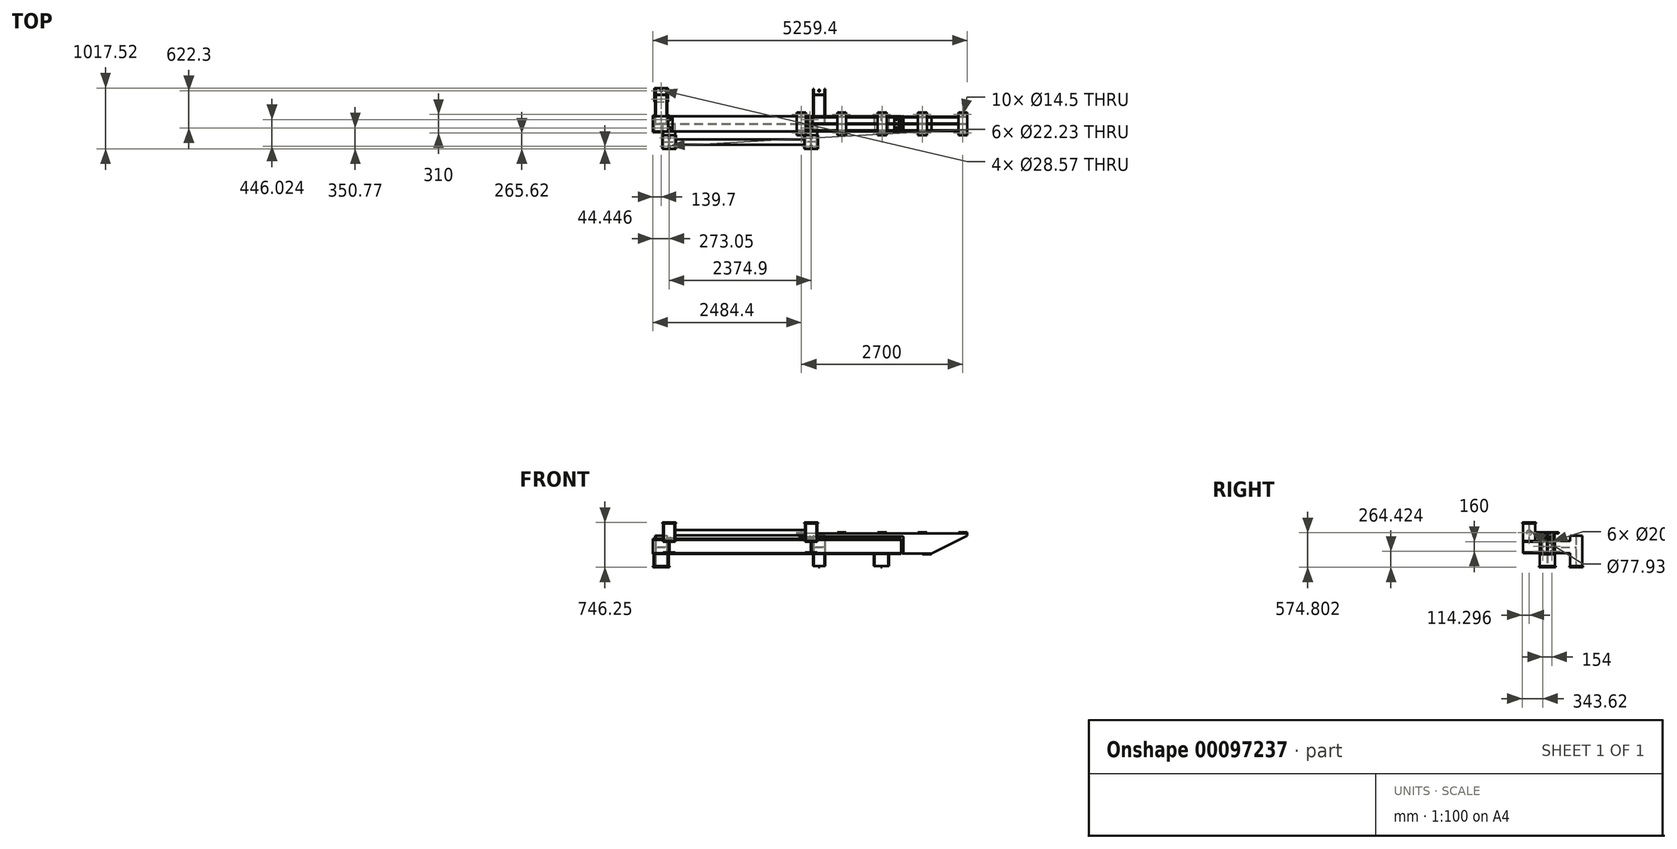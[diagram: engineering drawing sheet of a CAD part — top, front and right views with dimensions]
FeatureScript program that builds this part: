
annotation { "Feature Type Name" : "Feature", "Feature Type Description" : "" }
export const myFeature = defineFeature(function(context is Context, id is Id, definition is map)
    precondition{}
    {
        {
            var Q0;
            Q0=qCreatedBy(makeId("Top.planeOp"),FACE);
            var sketch = newSketch(context, id + "F0", { "sketchPlane" : qUnion([Q0])});
            skLineSegment(sketch, "E0.bottom", {"start": v(-1320.8, 241.3) * mm, "end": v(1320.8, 241.3) * mm, "construction": true});
            skLineSegment(sketch, "E0.top", {"start": v(-1320.8, -241.3) * mm, "end": v(1320.8, -241.3) * mm, "construction": true});
            skLineSegment(sketch, "E0.left", {"start": v(-1320.8, 241.3) * mm, "end": v(-1320.8, -241.3) * mm, "construction": true});
            skLineSegment(sketch, "E0.right", {"start": v(1320.8, 241.3) * mm, "end": v(1320.8, -241.3) * mm, "construction": true});
            skPoint(sketch, "E0.middle", {"position": v(0, 0) * mm});
            skLineSegment(sketch, "E1.bottom", {"start": v(-1435.1, 355.6) * mm, "end": v(-1206.5, 355.6) * mm});
            skLineSegment(sketch, "E1.top", {"start": v(-1435.1, 127) * mm, "end": v(-1206.5, 127) * mm});
            skLineSegment(sketch, "E1.left", {"start": v(-1435.1, 355.6) * mm, "end": v(-1435.1, 127) * mm});
            skLineSegment(sketch, "E1.right", {"start": v(-1206.5, 355.6) * mm, "end": v(-1206.5, 127) * mm});
            skPoint(sketch, "E1.middle", {"position": v(-1320.8, 241.3) * mm});
            skLineSegment(sketch, "E2", {"start": v(0, -413.23) * mm, "end": v(0, 639.03) * mm, "construction": true});
            skLineSegment(sketch, "E3", {"start": v(-1320.8, 355.6) * mm, "end": v(-1320.8, 127) * mm, "construction": true});
            skLineSegment(sketch, "E4", {"start": v(-1435.1, 241.3) * mm, "end": v(-1206.5, 241.3) * mm, "construction": true});
            skLineSegment(sketch, "E5.0", {"start": v(-1435.1, 311.15) * mm, "end": v(-1206.5, 311.15) * mm, "construction": true});
            skCircle(sketch, "E6", {"center": v(-1320.8, 311.15) * mm, "radius": 14.29 * mm});
            skCircle(sketch, "E7.MirrorC", {"center": v(-1320.8, 171.45) * mm, "radius": 14.29 * mm});
            skCircle(sketch, "E8.MirrorC", {"center": v(1320.8, 311.15) * mm, "radius": 14.29 * mm});
            skCircle(sketch, "E9.MirrorC", {"center": v(1320.8, 171.45) * mm, "radius": 14.29 * mm});
            skLineSegment(sketch, "E10.MirrorCS", {"start": v(1435.1, 311.15) * mm, "end": v(1206.5, 311.15) * mm, "construction": true});
            skLineSegment(sketch, "E11.MirrorCS", {"start": v(1435.1, 241.3) * mm, "end": v(1206.5, 241.3) * mm, "construction": true});
            skLineSegment(sketch, "E12.MirrorCS", {"start": v(1320.8, 355.6) * mm, "end": v(1320.8, 127) * mm, "construction": true});
            skLineSegment(sketch, "E13.MirrorCS", {"start": v(1435.1, 355.6) * mm, "end": v(1206.5, 355.6) * mm});
            skPoint(sketch, "E14.MirrorP", {"position": v(1320.8, 241.3) * mm});
            skLineSegment(sketch, "E15.MirrorCS", {"start": v(1206.5, 355.6) * mm, "end": v(1206.5, 127) * mm});
            skLineSegment(sketch, "E16.MirrorCS", {"start": v(1435.1, 127) * mm, "end": v(1206.5, 127) * mm});
            skLineSegment(sketch, "E17.MirrorCS", {"start": v(1435.1, 355.6) * mm, "end": v(1435.1, 127) * mm});
            skLineSegment(sketch, "E18.bottom", {"start": v(-1460.5, -381) * mm, "end": v(-1181.1, -381) * mm});
            skLineSegment(sketch, "E18.top", {"start": v(-1460.5, -101.6) * mm, "end": v(-1181.1, -101.6) * mm});
            skLineSegment(sketch, "E18.left", {"start": v(-1460.5, -381) * mm, "end": v(-1460.5, -101.6) * mm});
            skLineSegment(sketch, "E18.right", {"start": v(-1181.1, -381) * mm, "end": v(-1181.1, -101.6) * mm});
            skPoint(sketch, "E18.middle", {"position": v(-1320.8, -241.3) * mm});
            skLineSegment(sketch, "E19", {"start": v(-1320.8, -241.3) * mm, "end": v(-1460.5, -241.3) * mm, "construction": true});
            skLineSegment(sketch, "E20.0", {"start": v(-1320.8, -171.45) * mm, "end": v(-1460.5, -171.45) * mm, "construction": true});
            skCircle(sketch, "E21", {"center": v(-1320.8, -171.45) * mm, "radius": 14.29 * mm});
            skCircle(sketch, "E22.MirrorC", {"center": v(-1320.8, -311.15) * mm, "radius": 14.29 * mm});
            skLineSegment(sketch, "E23", {"start": v(-1320.8, -638.8) * mm, "end": v(-1320.8, -1011) * mm, "construction": true});
            skPoint(sketch, "E24.orphan", {"position": v(-1320.8, -381) * mm});
            skLineSegment(sketch, "E25.0", {"start": v(0, -638.8) * mm, "end": v(0, -1011) * mm, "construction": true});
            skLineSegment(sketch, "E26.0", {"start": v(1320.8, -638.8) * mm, "end": v(1320.8, -1011) * mm, "construction": true});
            skLineSegment(sketch, "E27.0", {"start": v(2362.2, -638.8) * mm, "end": v(2362.2, -1011) * mm, "construction": true});
            skLineSegment(sketch, "E28", {"start": v(-1320.8, -1011) * mm, "end": v(2362.2, -1011) * mm, "construction": true});
            skLineSegment(sketch, "E29", {"start": v(520.7, -1011) * mm, "end": v(520.7, -1354.57) * mm, "construction": true});
            skCircle(sketch, "E30.MirrorC", {"center": v(2362.2, -171.45) * mm, "radius": 14.29 * mm});
            skCircle(sketch, "E31.MirrorC", {"center": v(2362.2, -311.15) * mm, "radius": 14.29 * mm});
            skLineSegment(sketch, "E32.MirrorCS", {"start": v(2362.2, -171.45) * mm, "end": v(2501.9, -171.45) * mm, "construction": true});
            skLineSegment(sketch, "E33.MirrorCS", {"start": v(2501.9, -101.6) * mm, "end": v(2222.5, -101.6) * mm});
            skLineSegment(sketch, "E34.MirrorCS", {"start": v(2501.9, -381) * mm, "end": v(2222.5, -381) * mm});
            skLineSegment(sketch, "E35.MirrorCS", {"start": v(2362.2, -241.3) * mm, "end": v(2501.9, -241.3) * mm, "construction": true});
            skPoint(sketch, "E36.MirrorP", {"position": v(2362.2, -241.3) * mm});
            skLineSegment(sketch, "E37.MirrorCS", {"start": v(2222.5, -381) * mm, "end": v(2222.5, -101.6) * mm});
            skPoint(sketch, "E38.MirrorP", {"position": v(2362.2, -381) * mm});
            skLineSegment(sketch, "E39.MirrorCS", {"start": v(2501.9, -381) * mm, "end": v(2501.9, -101.6) * mm});
            skSolve(sketch);
        }
        {
            var Q0;
            Q0=makeQuery(id+"F0.imprint","IMPRINT",FACE,{"disambiguationData":[TD([[makeQuery(id+"F0.imprint","IMPRINT",EDGE,{"derivedFrom":sQuery(id+"F0.wireOp",EDGE,"E1.bottom")}),-1.0]])]});
            var Q1;
            Q1=makeQuery(id+"F0.imprint","IMPRINT",FACE,{"disambiguationData":[TD([[makeQuery(id+"F0.imprint","IMPRINT",EDGE,{"derivedFrom":sQuery(id+"F0.wireOp",EDGE,"E8.MirrorC")}),1.0]])]});
            var Q2;
            Q2=makeQuery(id+"F0.imprint","IMPRINT",FACE,{"disambiguationData":[TD([[makeQuery(id+"F0.imprint","IMPRINT",EDGE,{"derivedFrom":sQuery(id+"F0.wireOp",EDGE,"E30.MirrorC")}),1.0]])]});
            var Q3;
            Q3=makeQuery(id+"F0.imprint","IMPRINT",FACE,{"disambiguationData":[TD([[makeQuery(id+"F0.imprint","IMPRINT",EDGE,{"derivedFrom":sQuery(id+"F0.wireOp",EDGE,"E18.bottom")}),1.0]])]});
            extrude(context, id + "F1", {"entities" : qUnion([Q0, Q1, Q2, Q3]), "depth" : 19.05 * mm});
        }
        {
            var Q0;
            Q0=makeQuery(id+"F1.opExtrude","CAP_FACE",FACE,{"disambiguationData":[OSD([sQuery(id+"F0.wireOp",EDGE,"E1.bottom"),sQuery(id+"F0.wireOp",EDGE,"E1.top"),sQuery(id+"F0.wireOp",EDGE,"E1.left"),sQuery(id+"F0.wireOp",EDGE,"E1.right"),sQuery(id+"F0.wireOp",EDGE,"E6"),sQuery(id+"F0.wireOp",EDGE,"E7.MirrorC")])],"isStart":false});
            var sketch = newSketch(context, id + "F2", { "sketchPlane" : qUnion([Q0])});
            skLineSegment(sketch, "E40.0", {"start": v(-1435.1, 241.3) * mm, "end": v(-1206.5, 241.3) * mm, "construction": true});
            skLineSegment(sketch, "E41.0", {"start": v(-1320.8, 355.6) * mm, "end": v(-1320.8, 127) * mm, "construction": true});
            skLineSegment(sketch, "E42.bottom", {"start": v(-1422.4, 342.9) * mm, "end": v(-1411.35, 342.9) * mm});
            skLineSegment(sketch, "E42.top", {"start": v(-1422.4, 139.7) * mm, "end": v(-1411.35, 139.7) * mm});
            skLineSegment(sketch, "E42.left", {"start": v(-1422.4, 342.9) * mm, "end": v(-1422.4, 139.7) * mm});
            skLineSegment(sketch, "E42.right", {"start": v(-1219.2, 342.9) * mm, "end": v(-1219.2, 139.7) * mm, "construction": true});
            skPoint(sketch, "E42.middle", {"position": v(-1320.8, 241.3) * mm});
            skLineSegment(sketch, "E43.0", {"start": v(-1411.35, 342.9) * mm, "end": v(-1411.35, 251.27) * mm});
            skLineSegment(sketch, "E44.trimOffspring", {"start": v(-1405, 237.68) * mm, "end": v(-1320.8, 237.68) * mm});
            skLineSegment(sketch, "E45.MirrorCS", {"start": v(-1405, 244.92) * mm, "end": v(-1320.8, 244.92) * mm});
            skLineSegment(sketch, "E46.trimOffspring", {"start": v(-1411.35, 231.33) * mm, "end": v(-1411.35, 139.7) * mm});
            skPoint(sketch, "E47.visualSharp", {"position": v(-1411.35, 244.92) * mm});
            skArc(sketch, "E47.filletArc", {"start": v(-1411.35, 251.27) * mm, "mid": v(-1409.5, 246.78) * mm, "end": v(-1405, 244.92) * mm});
            skPoint(sketch, "E48.visualSharp", {"position": v(-1411.35, 237.68) * mm});
            skArc(sketch, "E48.filletArc", {"start": v(-1405, 237.68) * mm, "mid": v(-1409.5, 235.82) * mm, "end": v(-1411.35, 231.33) * mm});
            skArc(sketch, "E49.MirrorCS", {"start": v(-1236.6, 237.68) * mm, "mid": v(-1232.1, 235.82) * mm, "end": v(-1230.25, 231.33) * mm});
            skArc(sketch, "E50.MirrorCS", {"start": v(-1230.25, 251.27) * mm, "mid": v(-1232.1, 246.78) * mm, "end": v(-1236.6, 244.92) * mm});
            skPoint(sketch, "E51.MirrorP", {"position": v(-1230.25, 237.68) * mm});
            skPoint(sketch, "E52.MirrorP", {"position": v(-1230.25, 244.92) * mm});
            skLineSegment(sketch, "E53.MirrorCS", {"start": v(-1230.25, 342.9) * mm, "end": v(-1230.25, 251.27) * mm});
            skLineSegment(sketch, "E54.MirrorCS", {"start": v(-1236.6, 237.68) * mm, "end": v(-1320.8, 237.68) * mm});
            skLineSegment(sketch, "E55.MirrorCS", {"start": v(-1236.6, 244.92) * mm, "end": v(-1320.8, 244.92) * mm});
            skLineSegment(sketch, "E56.MirrorCS", {"start": v(-1219.2, 139.7) * mm, "end": v(-1230.25, 139.7) * mm});
            skLineSegment(sketch, "E57.MirrorCS", {"start": v(-1230.25, 231.33) * mm, "end": v(-1230.25, 139.7) * mm});
            skLineSegment(sketch, "E58.MirrorCS", {"start": v(-1219.2, 342.9) * mm, "end": v(-1230.25, 342.9) * mm});
            skLineSegment(sketch, "E59.MirrorCS", {"start": v(-1219.2, 342.9) * mm, "end": v(-1219.2, 139.7) * mm});
            skLineSegment(sketch, "E60.0", {"start": v(0, -413.23) * mm, "end": v(0, 639.03) * mm, "construction": true});
            skArc(sketch, "E61.MirrorCS", {"start": v(1411.35, 251.27) * mm, "mid": v(1409.5, 246.78) * mm, "end": v(1405, 244.92) * mm});
            skArc(sketch, "E62.MirrorCS", {"start": v(1405, 237.68) * mm, "mid": v(1409.5, 235.82) * mm, "end": v(1411.35, 231.33) * mm});
            skLineSegment(sketch, "E63.MirrorCS", {"start": v(1236.6, 244.92) * mm, "end": v(1320.8, 244.92) * mm});
            skArc(sketch, "E64.MirrorCS", {"start": v(1236.6, 237.68) * mm, "mid": v(1232.1, 235.82) * mm, "end": v(1230.25, 231.33) * mm});
            skLineSegment(sketch, "E65.MirrorCS", {"start": v(1422.4, 139.7) * mm, "end": v(1411.35, 139.7) * mm});
            skLineSegment(sketch, "E66.MirrorCS", {"start": v(1422.4, 342.9) * mm, "end": v(1411.35, 342.9) * mm});
            skArc(sketch, "E67.MirrorCS", {"start": v(1230.25, 251.27) * mm, "mid": v(1232.1, 246.78) * mm, "end": v(1236.6, 244.92) * mm});
            skLineSegment(sketch, "E68.MirrorCS", {"start": v(1236.6, 237.68) * mm, "end": v(1320.8, 237.68) * mm});
            skLineSegment(sketch, "E69.MirrorCS", {"start": v(1435.1, 241.3) * mm, "end": v(1206.5, 241.3) * mm, "construction": true});
            skLineSegment(sketch, "E70.MirrorCS", {"start": v(1405, 237.68) * mm, "end": v(1320.8, 237.68) * mm});
            skLineSegment(sketch, "E71.MirrorCS", {"start": v(1219.2, 342.9) * mm, "end": v(1230.25, 342.9) * mm});
            skLineSegment(sketch, "E72.MirrorCS", {"start": v(1219.2, 139.7) * mm, "end": v(1230.25, 139.7) * mm});
            skLineSegment(sketch, "E73.MirrorCS", {"start": v(1411.35, 342.9) * mm, "end": v(1411.35, 251.27) * mm});
            skLineSegment(sketch, "E74.MirrorCS", {"start": v(1405, 244.92) * mm, "end": v(1320.8, 244.92) * mm});
            skLineSegment(sketch, "E75.MirrorCS", {"start": v(1411.35, 231.33) * mm, "end": v(1411.35, 139.7) * mm});
            skPoint(sketch, "E76.MirrorP", {"position": v(1411.35, 237.68) * mm});
            skPoint(sketch, "E77.MirrorP", {"position": v(1320.8, 241.3) * mm});
            skLineSegment(sketch, "E78.MirrorCS", {"start": v(1219.2, 342.9) * mm, "end": v(1219.2, 139.7) * mm, "construction": true});
            skLineSegment(sketch, "E79.MirrorCS", {"start": v(1422.4, 342.9) * mm, "end": v(1422.4, 139.7) * mm});
            skPoint(sketch, "E80.MirrorP", {"position": v(1230.25, 237.68) * mm});
            skLineSegment(sketch, "E81.MirrorCS", {"start": v(1320.8, 355.6) * mm, "end": v(1320.8, 127) * mm, "construction": true});
            skPoint(sketch, "E82.MirrorP", {"position": v(1411.35, 244.92) * mm});
            skLineSegment(sketch, "E83.MirrorCS", {"start": v(1219.2, 342.9) * mm, "end": v(1219.2, 139.7) * mm});
            skLineSegment(sketch, "E84.MirrorCS", {"start": v(1230.25, 231.33) * mm, "end": v(1230.25, 139.7) * mm});
            skLineSegment(sketch, "E85.MirrorCS", {"start": v(1230.25, 342.9) * mm, "end": v(1230.25, 251.27) * mm});
            skPoint(sketch, "E86.MirrorP", {"position": v(1230.25, 244.92) * mm});
            skSolve(sketch);
        }
        {
            var Q0;
            Q0=qSketchRegion(id+"F2",true);
            extrude(context, id + "F3", {"entities" : qUnion([Q0]), "depth" : 504.95 * mm});
        }
        {
            var Q0;
            Q0=makeQuery(id+"F3.opExtrude","SWEPT_FACE",FACE,{"disambiguationData":[OSD([sQuery(id+"F2.wireOp",EDGE,"E79.MirrorCS")])]});
            var sketch = newSketch(context, id + "F4", { "sketchPlane" : qUnion([Q0])});
            skLineSegment(sketch, "E87.bottom", {"start": v(139.7, 524) * mm, "end": v(342.9, 524) * mm});
            skLineSegment(sketch, "E87.top", {"start": v(139.7, 727.2) * mm, "end": v(342.9, 727.2) * mm});
            skLineSegment(sketch, "E87.left", {"start": v(139.7, 524) * mm, "end": v(139.7, 535.05) * mm});
            skLineSegment(sketch, "E87.right", {"start": v(342.9, 524) * mm, "end": v(342.9, 535.05) * mm});
            skLineSegment(sketch, "E88", {"start": v(241.3, 727.2) * mm, "end": v(241.3, 524) * mm, "construction": true});
            skLineSegment(sketch, "E89.0", {"start": v(237.68, 709.8) * mm, "end": v(237.68, 541.4) * mm});
            skLineSegment(sketch, "E90.MirrorCS", {"start": v(244.92, 709.8) * mm, "end": v(244.92, 541.4) * mm});
            skLineSegment(sketch, "E91.0", {"start": v(139.7, 716.15) * mm, "end": v(231.33, 716.15) * mm});
            skLineSegment(sketch, "E92.0", {"start": v(139.7, 535.05) * mm, "end": v(231.33, 535.05) * mm});
            skLineSegment(sketch, "E93.trimOffspring", {"start": v(251.27, 716.15) * mm, "end": v(342.9, 716.15) * mm});
            skLineSegment(sketch, "E94.trimOffspring", {"start": v(251.27, 535.05) * mm, "end": v(342.9, 535.05) * mm});
            skLineSegment(sketch, "E95.trimOffspring", {"start": v(139.7, 716.15) * mm, "end": v(139.7, 727.2) * mm});
            skLineSegment(sketch, "E96.trimOffspring", {"start": v(342.9, 716.15) * mm, "end": v(342.9, 727.2) * mm});
            skPoint(sketch, "E97.newPointB", {"position": v(237.68, 524) * mm});
            skArc(sketch, "E97.filletArc", {"start": v(231.33, 535.05) * mm, "mid": v(235.82, 536.91) * mm, "end": v(237.68, 541.4) * mm});
            skPoint(sketch, "E98.newPointA", {"position": v(244.92, 524) * mm});
            skArc(sketch, "E98.filletArc", {"start": v(244.92, 541.4) * mm, "mid": v(246.78, 536.91) * mm, "end": v(251.27, 535.05) * mm});
            skPoint(sketch, "E99.newPointA", {"position": v(237.68, 727.2) * mm});
            skArc(sketch, "E99.filletArc", {"start": v(237.68, 709.8) * mm, "mid": v(235.82, 714.3) * mm, "end": v(231.33, 716.15) * mm});
            skPoint(sketch, "E100.newPointA", {"position": v(244.92, 727.2) * mm});
            skArc(sketch, "E100.filletArc", {"start": v(251.27, 716.15) * mm, "mid": v(246.78, 714.3) * mm, "end": v(244.92, 709.8) * mm});
            skSolve(sketch);
        }
        {
            var Q0;
            Q0=qSketchRegion(id+"F4",true);
            var Q1;
            Q1=makeQuery(id+"F3.opExtrude","SWEPT_FACE",FACE,{"disambiguationData":[OSD([sQuery(id+"F2.wireOp",EDGE,"E42.left")])]});
            extrude(context, id + "F5", {"entities" : qUnion([Q0]), "endBound" : BoundingType.UP_TO_SURFACE, "oppositeDirection" : true, "endBoundEntityFace" : qUnion([Q1]), "depth" : 25.4 * mm});
        }
        {
            var Q0;
            Q0=makeQuery(id+"F5.opExtrude","SWEPT_FACE",FACE,{"disambiguationData":[OSD([sQuery(id+"F4.wireOp",EDGE,"E87.top")])]});
            var sketch = newSketch(context, id + "F6", { "sketchPlane" : qUnion([Q0])});
            skLineSegment(sketch, "E101.0", {"start": v(0, -413.23) * mm, "end": v(0, 639.03) * mm, "construction": true});
            skLineSegment(sketch, "E102.0", {"start": v(-1187.45, -413.23) * mm, "end": v(-1187.45, 639.03) * mm, "construction": true});
            skLineSegment(sketch, "E103.0", {"start": v(-1225.55, 139.7) * mm, "end": v(-1225.55, 342.9) * mm});
            skLineSegment(sketch, "E104.0", {"start": v(-1098.55, 139.7) * mm, "end": v(-1098.55, 342.9) * mm});
            skLineSegment(sketch, "E105.0", {"start": v(-1422.4, 342.9) * mm, "end": v(1422.4, 342.9) * mm, "construction": true});
            skLineSegment(sketch, "E106.0.0", {"start": v(1225.55, 342.9) * mm, "end": v(-1225.55, 342.9) * mm});
            skLineSegment(sketch, "E106.0.1", {"start": v(-1422.4, 342.9) * mm, "end": v(-1422.4, 139.7) * mm});
            skLineSegment(sketch, "E106.0.2", {"start": v(-1225.55, 139.7) * mm, "end": v(-1098.55, 139.7) * mm});
            skLineSegment(sketch, "E106.0.3", {"start": v(1422.4, 139.7) * mm, "end": v(1422.4, 342.9) * mm});
            skLineSegment(sketch, "E107.trimOffspring", {"start": v(0, 139.7) * mm, "end": v(1225.55, 139.7) * mm});
            skLineSegment(sketch, "E108.0", {"start": v(-1320.8, 241.3) * mm, "end": v(1320.8, 241.3) * mm, "construction": true});
            skLineSegment(sketch, "E109.0", {"start": v(-1320.8, 311.15) * mm, "end": v(1320.8, 311.15) * mm, "construction": true});
            skCircle(sketch, "E110", {"center": v(-1187.45, 311.15) * mm, "radius": 11.11 * mm});
            skCircle(sketch, "E111.MirrorC", {"center": v(-1187.45, 171.45) * mm, "radius": 11.11 * mm});
            skCircle(sketch, "E112.MirrorC", {"center": v(1187.45, 311.15) * mm, "radius": 11.11 * mm});
            skCircle(sketch, "E113.MirrorC", {"center": v(1187.45, 171.45) * mm, "radius": 11.11 * mm});
            skLineSegment(sketch, "E114.MirrorCS", {"start": v(1225.55, 139.7) * mm, "end": v(1098.55, 139.7) * mm});
            skLineSegment(sketch, "E115.MirrorCS", {"start": v(1225.55, 139.7) * mm, "end": v(1225.55, 342.9) * mm});
            skLineSegment(sketch, "E116.MirrorCS", {"start": v(1098.55, 139.7) * mm, "end": v(1098.55, 342.9) * mm});
            skSolve(sketch);
        }
        {
            var Q0;
            Q0=qSketchRegion(id+"F6",true);
            extrude(context, id + "F7", {"entities" : qUnion([Q0]), "operationType" : NewBodyOperationType.ADD, "depth" : 19.05 * mm});
        }
        {
            var Q0;
            Q0=makeQuery(id+"F3.opExtrude","SWEPT_FACE",FACE,{"disambiguationData":[OSD([sQuery(id+"F2.wireOp",EDGE,"E44.trimOffspring"),sQuery(id+"F2.wireOp",EDGE,"E54.MirrorCS")])]});
            var sketch = newSketch(context, id + "F8", { "sketchPlane" : qUnion([Q0])});
            skLineSegment(sketch, "E117.0", {"start": v(-1460.5, 0) * mm, "end": v(-1181.1, 0) * mm, "construction": true});
            skLineSegment(sketch, "E118", {"start": v(-1320.8, 0) * mm, "end": v(-1320.8, 868.41) * mm, "construction": true});
            skLineSegment(sketch, "E119.0", {"start": v(-1422.4, 231.65) * mm, "end": v(-1411.35, 231.65) * mm});
            skLineSegment(sketch, "E120.0", {"start": v(-1422.4, 434.85) * mm, "end": v(-1411.35, 434.85) * mm});
            skLineSegment(sketch, "E121", {"start": v(-1422.4, 434.85) * mm, "end": v(-1422.4, 231.65) * mm});
            skLineSegment(sketch, "E122.0", {"start": v(-1411.35, 434.85) * mm, "end": v(-1411.35, 342.77) * mm});
            skLineSegment(sketch, "E123", {"start": v(-1411.35, 333.25) * mm, "end": v(-1320.8, 333.25) * mm, "construction": true});
            skLineSegment(sketch, "E124.0", {"start": v(-1405, 336.42) * mm, "end": v(-1320.8, 336.42) * mm});
            skLineSegment(sketch, "E125.MirrorCS", {"start": v(-1410.08, 330.07) * mm, "end": v(-1320.8, 330.07) * mm});
            skLineSegment(sketch, "E126.trimOffspring", {"start": v(-1411.35, 328.8) * mm, "end": v(-1411.35, 231.65) * mm});
            skPoint(sketch, "E127.newPointA", {"position": v(-1411.35, 336.42) * mm});
            skArc(sketch, "E127.filletArc", {"start": v(-1411.35, 342.77) * mm, "mid": v(-1409.5, 338.28) * mm, "end": v(-1405, 336.42) * mm});
            skPoint(sketch, "E128.visualSharp", {"position": v(-1411.35, 330.07) * mm});
            skArc(sketch, "E128.filletArc", {"start": v(-1410.08, 330.07) * mm, "mid": v(-1410.98, 329.7) * mm, "end": v(-1411.35, 328.8) * mm});
            skArc(sketch, "E129.MirrorCS", {"start": v(-1231.52, 330.07) * mm, "mid": v(-1230.62, 329.7) * mm, "end": v(-1230.25, 328.8) * mm});
            skArc(sketch, "E130.MirrorCS", {"start": v(-1230.25, 342.77) * mm, "mid": v(-1232.1, 338.28) * mm, "end": v(-1236.6, 336.42) * mm});
            skLineSegment(sketch, "E131.MirrorCS", {"start": v(-1219.2, 231.65) * mm, "end": v(-1230.25, 231.65) * mm});
            skLineSegment(sketch, "E132.MirrorCS", {"start": v(-1219.2, 434.85) * mm, "end": v(-1230.25, 434.85) * mm});
            skPoint(sketch, "E133.MirrorP", {"position": v(-1230.25, 336.42) * mm});
            skPoint(sketch, "E134.MirrorP", {"position": v(-1230.25, 330.07) * mm});
            skLineSegment(sketch, "E135.MirrorCS", {"start": v(-1230.25, 328.8) * mm, "end": v(-1230.25, 231.65) * mm});
            skLineSegment(sketch, "E136.MirrorCS", {"start": v(-1231.52, 330.07) * mm, "end": v(-1320.8, 330.07) * mm});
            skLineSegment(sketch, "E137.MirrorCS", {"start": v(-1219.2, 434.85) * mm, "end": v(-1219.2, 231.65) * mm});
            skLineSegment(sketch, "E138.MirrorCS", {"start": v(-1230.25, 434.85) * mm, "end": v(-1230.25, 342.77) * mm});
            skLineSegment(sketch, "E139.MirrorCS", {"start": v(-1230.25, 333.25) * mm, "end": v(-1320.8, 333.25) * mm, "construction": true});
            skLineSegment(sketch, "E140.MirrorCS", {"start": v(-1236.6, 336.42) * mm, "end": v(-1320.8, 336.42) * mm});
            skLineSegment(sketch, "E141", {"start": v(0, -179.83) * mm, "end": v(0, 965.66) * mm, "construction": true});
            skArc(sketch, "E142.MirrorCS", {"start": v(1411.35, 342.77) * mm, "mid": v(1409.5, 338.28) * mm, "end": v(1405, 336.42) * mm});
            skArc(sketch, "E143.MirrorCS", {"start": v(1410.08, 330.07) * mm, "mid": v(1410.98, 329.7) * mm, "end": v(1411.35, 328.8) * mm});
            skArc(sketch, "E144.MirrorCS", {"start": v(1230.25, 342.77) * mm, "mid": v(1232.1, 338.28) * mm, "end": v(1236.6, 336.42) * mm});
            skArc(sketch, "E145.MirrorCS", {"start": v(1231.52, 330.07) * mm, "mid": v(1230.62, 329.7) * mm, "end": v(1230.25, 328.8) * mm});
            skLineSegment(sketch, "E146.MirrorCS", {"start": v(1411.35, 333.25) * mm, "end": v(1320.8, 333.25) * mm, "construction": true});
            skLineSegment(sketch, "E147.MirrorCS", {"start": v(1219.2, 231.65) * mm, "end": v(1230.25, 231.65) * mm});
            skLineSegment(sketch, "E148.MirrorCS", {"start": v(1219.2, 434.85) * mm, "end": v(1230.25, 434.85) * mm});
            skLineSegment(sketch, "E149.MirrorCS", {"start": v(1422.4, 231.65) * mm, "end": v(1411.35, 231.65) * mm});
            skLineSegment(sketch, "E150.MirrorCS", {"start": v(1422.4, 434.85) * mm, "end": v(1411.35, 434.85) * mm});
            skLineSegment(sketch, "E151.MirrorCS", {"start": v(1405, 336.42) * mm, "end": v(1320.8, 336.42) * mm});
            skLineSegment(sketch, "E152.MirrorCS", {"start": v(1410.08, 330.07) * mm, "end": v(1320.8, 330.07) * mm});
            skLineSegment(sketch, "E153.MirrorCS", {"start": v(1230.25, 333.25) * mm, "end": v(1320.8, 333.25) * mm, "construction": true});
            skLineSegment(sketch, "E154.MirrorCS", {"start": v(1231.52, 330.07) * mm, "end": v(1320.8, 330.07) * mm});
            skLineSegment(sketch, "E155.MirrorCS", {"start": v(1236.6, 336.42) * mm, "end": v(1320.8, 336.42) * mm});
            skLineSegment(sketch, "E156.MirrorCS", {"start": v(1411.35, 328.8) * mm, "end": v(1411.35, 231.65) * mm});
            skPoint(sketch, "E157.MirrorP", {"position": v(1411.35, 330.07) * mm});
            skPoint(sketch, "E158.MirrorP", {"position": v(1411.35, 336.42) * mm});
            skLineSegment(sketch, "E159.MirrorCS", {"start": v(1422.4, 434.85) * mm, "end": v(1422.4, 231.65) * mm});
            skLineSegment(sketch, "E160.MirrorCS", {"start": v(1411.35, 434.85) * mm, "end": v(1411.35, 342.77) * mm});
            skLineSegment(sketch, "E161.MirrorCS", {"start": v(1230.25, 434.85) * mm, "end": v(1230.25, 342.77) * mm});
            skLineSegment(sketch, "E162.MirrorCS", {"start": v(1230.25, 328.8) * mm, "end": v(1230.25, 231.65) * mm});
            skPoint(sketch, "E163.MirrorP", {"position": v(1230.25, 330.07) * mm});
            skPoint(sketch, "E164.MirrorP", {"position": v(1230.25, 336.42) * mm});
            skLineSegment(sketch, "E165.MirrorCS", {"start": v(1219.2, 434.85) * mm, "end": v(1219.2, 231.65) * mm});
            skSolve(sketch);
        }
        {
            var Q0;
            Q0=qSketchRegion(id+"F8",true);
            extrude(context, id + "F9", {"entities" : qUnion([Q0]), "operationType" : NewBodyOperationType.ADD, "depth" : 482.6 * mm});
        }
        {
            var Q0;
            Q0=qCreatedBy(makeId("Right.planeOp"),FACE);
            cPlane(context, id + "F10", {"entities" : qUnion([Q0]), "cplaneType" : CPlaneType.OFFSET, "offset" : 2692.4 * mm, "width" : 152.4 * mm, "height" : 152.4 * mm});
        }
        {
            var Q0;
            Q0=qCreatedBy(id+"F10.planeOp",FACE);
            var sketch = newSketch(context, id + "F11", { "sketchPlane" : qUnion([Q0])});
            skLineSegment(sketch, "E166.0", {"start": v(-381, 19.05) * mm, "end": v(-101.6, 19.05) * mm, "construction": true});
            skLineSegment(sketch, "E167", {"start": v(-241.3, 19.05) * mm, "end": v(-241.3, 468.37) * mm, "construction": true});
            skLineSegment(sketch, "E168.0", {"start": v(-381, 217.42) * mm, "end": v(-101.6, 217.42) * mm, "construction": true});
            skLineSegment(sketch, "E169.bottom", {"start": v(-368.3, 217.42) * mm, "end": v(-114.3, 217.42) * mm});
            skLineSegment(sketch, "E169.top", {"start": v(-368.3, 471.42) * mm, "end": v(-114.3, 471.42) * mm});
            skLineSegment(sketch, "E169.left", {"start": v(-368.3, 217.42) * mm, "end": v(-368.3, 231.65) * mm});
            skLineSegment(sketch, "E169.right", {"start": v(-114.3, 217.42) * mm, "end": v(-114.3, 231.65) * mm});
            skLineSegment(sketch, "E170.0", {"start": v(-368.3, 457.2) * mm, "end": v(-254, 457.2) * mm});
            skLineSegment(sketch, "E171.0", {"start": v(-368.3, 231.65) * mm, "end": v(-254, 231.65) * mm});
            skLineSegment(sketch, "E172.0", {"start": v(-234.95, 238) * mm, "end": v(-234.95, 450.85) * mm});
            skLineSegment(sketch, "E173.MirrorCS", {"start": v(-247.65, 238) * mm, "end": v(-247.65, 450.85) * mm});
            skLineSegment(sketch, "E174.trimOffspring", {"start": v(-368.3, 457.2) * mm, "end": v(-368.3, 471.42) * mm});
            skLineSegment(sketch, "E175.trimOffspring", {"start": v(-114.3, 457.2) * mm, "end": v(-114.3, 471.42) * mm});
            skLineSegment(sketch, "E176.trimOffspring", {"start": v(-228.6, 457.2) * mm, "end": v(-114.3, 457.2) * mm});
            skLineSegment(sketch, "E177.trimOffspring", {"start": v(-228.6, 231.65) * mm, "end": v(-114.3, 231.65) * mm});
            skPoint(sketch, "E178.newPointB", {"position": v(-247.65, 468.37) * mm});
            skArc(sketch, "E178.filletArc", {"start": v(-247.65, 450.85) * mm, "mid": v(-249.5, 455.34) * mm, "end": v(-254, 457.2) * mm});
            skPoint(sketch, "E179.newPointB", {"position": v(-234.95, 468.37) * mm});
            skArc(sketch, "E179.filletArc", {"start": v(-228.6, 457.2) * mm, "mid": v(-233.1, 455.34) * mm, "end": v(-234.95, 450.85) * mm});
            skPoint(sketch, "E180.newPointB", {"position": v(-234.95, 19.05) * mm});
            skArc(sketch, "E180.filletArc", {"start": v(-234.95, 238) * mm, "mid": v(-233.1, 233.5) * mm, "end": v(-228.6, 231.65) * mm});
            skPoint(sketch, "E181.newPointA", {"position": v(-247.65, 19.05) * mm});
            skArc(sketch, "E181.filletArc", {"start": v(-254, 231.65) * mm, "mid": v(-249.5, 233.5) * mm, "end": v(-247.65, 238) * mm});
            skSolve(sketch);
        }
        {
            var Q0;
            Q0=qSketchRegion(id+"F11",true);
            extrude(context, id + "F12", {"entities" : qUnion([Q0]), "oppositeDirection" : true, "depth" : 4152.9 * mm});
        }
        {
            var Q0;
            Q0=makeQuery(id+"F1.opExtrude","CAP_FACE",FACE,{"disambiguationData":[OSD([sQuery(id+"F0.wireOp",EDGE,"E18.bottom"),sQuery(id+"F0.wireOp",EDGE,"E18.top"),sQuery(id+"F0.wireOp",EDGE,"E18.left"),sQuery(id+"F0.wireOp",EDGE,"E18.right"),sQuery(id+"F0.wireOp",EDGE,"E21"),sQuery(id+"F0.wireOp",EDGE,"E22.MirrorC")])],"isStart":false});
            var sketch = newSketch(context, id + "F13", { "sketchPlane" : qUnion([Q0])});
            skLineSegment(sketch, "E182.bottom", {"start": v(-1447.8, -114.3) * mm, "end": v(-1433.58, -114.3) * mm});
            skLineSegment(sketch, "E182.top", {"start": v(-1447.8, -368.3) * mm, "end": v(-1433.58, -368.3) * mm});
            skLineSegment(sketch, "E182.left", {"start": v(-1447.8, -114.3) * mm, "end": v(-1447.8, -368.3) * mm});
            skLineSegment(sketch, "E182.right", {"start": v(-1193.8, -114.3) * mm, "end": v(-1193.8, -368.3) * mm});
            skPoint(sketch, "E182.middle", {"position": v(-1320.8, -241.3) * mm});
            skLineSegment(sketch, "E183.0", {"start": v(-1433.58, -114.3) * mm, "end": v(-1433.58, -236.98) * mm});
            skLineSegment(sketch, "E184.0", {"start": v(-1208.02, -114.3) * mm, "end": v(-1208.02, -236.98) * mm});
            skLineSegment(sketch, "E185.trimOffspring", {"start": v(-1208.02, -114.3) * mm, "end": v(-1193.8, -114.3) * mm});
            skLineSegment(sketch, "E186.trimOffspring", {"start": v(-1208.02, -368.3) * mm, "end": v(-1193.8, -368.3) * mm});
            skLineSegment(sketch, "E187.0", {"start": v(-1208.02, -236.98) * mm, "end": v(-1433.58, -236.98) * mm});
            skLineSegment(sketch, "E188.MirrorCS", {"start": v(-1208.02, -245.62) * mm, "end": v(-1433.58, -245.62) * mm});
            skPoint(sketch, "E189.orphan", {"position": v(-1460.5, -236.98) * mm});
            skPoint(sketch, "E190.orphan", {"position": v(-1460.5, -245.62) * mm});
            skLineSegment(sketch, "E191.trimOffspring", {"start": v(-1433.58, -245.62) * mm, "end": v(-1433.58, -368.3) * mm});
            skPoint(sketch, "E192.orphan", {"position": v(-1320.8, -236.98) * mm});
            skPoint(sketch, "E193.orphan", {"position": v(-1320.8, -245.62) * mm});
            skLineSegment(sketch, "E194.trimOffspring", {"start": v(-1208.02, -245.62) * mm, "end": v(-1208.02, -368.3) * mm});
            skLineSegment(sketch, "E195.MirrorCS", {"start": v(2489.2, -368.3) * mm, "end": v(2474.98, -368.3) * mm});
            skLineSegment(sketch, "E196.MirrorCS", {"start": v(2489.2, -114.3) * mm, "end": v(2474.98, -114.3) * mm});
            skLineSegment(sketch, "E197.MirrorCS", {"start": v(2249.42, -368.3) * mm, "end": v(2235.2, -368.3) * mm});
            skLineSegment(sketch, "E198.MirrorCS", {"start": v(2249.42, -114.3) * mm, "end": v(2235.2, -114.3) * mm});
            skPoint(sketch, "E199.MirrorP", {"position": v(2362.2, -245.62) * mm});
            skPoint(sketch, "E200.MirrorP", {"position": v(2362.2, -236.98) * mm});
            skLineSegment(sketch, "E201.MirrorCS", {"start": v(2249.42, -245.62) * mm, "end": v(2474.98, -245.62) * mm});
            skPoint(sketch, "E202.MirrorP", {"position": v(2501.9, -236.98) * mm});
            skLineSegment(sketch, "E203.MirrorCS", {"start": v(2249.42, -236.98) * mm, "end": v(2474.98, -236.98) * mm});
            skPoint(sketch, "E204.MirrorP", {"position": v(2362.2, -241.3) * mm});
            skPoint(sketch, "E205.MirrorP", {"position": v(2501.9, -245.62) * mm});
            skLineSegment(sketch, "E206.MirrorCS", {"start": v(2249.42, -245.62) * mm, "end": v(2249.42, -368.3) * mm});
            skLineSegment(sketch, "E207.MirrorCS", {"start": v(2474.98, -245.62) * mm, "end": v(2474.98, -368.3) * mm});
            skLineSegment(sketch, "E208.MirrorCS", {"start": v(2249.42, -114.3) * mm, "end": v(2249.42, -236.98) * mm});
            skLineSegment(sketch, "E209.MirrorCS", {"start": v(2474.98, -114.3) * mm, "end": v(2474.98, -236.98) * mm});
            skLineSegment(sketch, "E210.MirrorCS", {"start": v(2235.2, -114.3) * mm, "end": v(2235.2, -368.3) * mm});
            skLineSegment(sketch, "E211.MirrorCS", {"start": v(2489.2, -114.3) * mm, "end": v(2489.2, -368.3) * mm});
            skSolve(sketch);
        }
        {
            var Q0;
            Q0=qSketchRegion(id+"F13",true);
            extrude(context, id + "F14", {"entities" : qUnion([Q0]), "depth" : 198.37 * mm});
        }
        {
            var Q0;
            Q0=makeQuery(id+"F12.opExtrude","SWEPT_FACE",FACE,{"disambiguationData":[OSD([sQuery(id+"F11.wireOp",EDGE,"E169.top")])]});
            var sketch = newSketch(context, id + "F15", { "sketchPlane" : qUnion([Q0])});
            skLineSegment(sketch, "E212.0", {"start": v(-1615.4, -241.3) * mm, "end": v(2831.5, -241.3) * mm, "construction": true});
            skLineSegment(sketch, "E213.0", {"start": v(0, -413.23) * mm, "end": v(0, 639.03) * mm, "construction": true});
            skPoint(sketch, "E214.orphan", {"position": v(-1320.8, -241.3) * mm});
            skLineSegment(sketch, "E215.0", {"start": v(-1168.4, -689.85) * mm, "end": v(-1168.4, 639.03) * mm, "construction": true});
            skLineSegment(sketch, "E216.0", {"start": v(-1130.3, -355.6) * mm, "end": v(-1130.3, -127) * mm});
            skLineSegment(sketch, "E217.0", {"start": v(-1206.5, -127) * mm, "end": v(-1130.3, -127) * mm});
            skLineSegment(sketch, "E218.0", {"start": v(-1615.4, -171.45) * mm, "end": v(2831.5, -171.45) * mm, "construction": true});
            skLineSegment(sketch, "E219.MirrorCS", {"start": v(-1206.5, -355.6) * mm, "end": v(-1130.3, -355.6) * mm});
            skLineSegment(sketch, "E220.MirrorCS", {"start": v(-1206.5, -355.6) * mm, "end": v(-1206.5, -127) * mm});
            skPoint(sketch, "E221.orphan", {"position": v(-1130.3, 639.03) * mm});
            skPoint(sketch, "E222.orphan", {"position": v(-1206.5, 639.03) * mm});
            skPoint(sketch, "E223.orphan", {"position": v(-1615.4, -127) * mm});
            skPoint(sketch, "E224.orphan", {"position": v(-1615.4, -355.6) * mm});
            skPoint(sketch, "E225.orphan", {"position": v(-1206.5, -689.85) * mm});
            skPoint(sketch, "E226.orphan", {"position": v(-1130.3, -689.85) * mm});
            skCircle(sketch, "E227", {"center": v(-1168.4, -171.45) * mm, "radius": 11.11 * mm});
            skCircle(sketch, "E228.MirrorC", {"center": v(-1168.4, -311.15) * mm, "radius": 11.11 * mm});
            skLineSegment(sketch, "E229.1.0.0", {"start": v(1130.3, -355.6) * mm, "end": v(1130.3, -127) * mm});
            skLineSegment(sketch, "E229.1.0.1", {"start": v(1130.3, -355.6) * mm, "end": v(1206.5, -355.6) * mm});
            skLineSegment(sketch, "E229.1.0.2", {"start": v(1130.3, -127) * mm, "end": v(1206.5, -127) * mm});
            skLineSegment(sketch, "E229.1.0.3", {"start": v(1206.5, -355.6) * mm, "end": v(1206.5, -127) * mm});
            skCircle(sketch, "E229.1.0.4", {"center": v(1168.4, -171.45) * mm, "radius": 11.11 * mm});
            skCircle(sketch, "E229.1.0.5", {"center": v(1168.4, -311.15) * mm, "radius": 11.11 * mm});
            skLineSegment(sketch, "E229.direction1", {"start": v(-1206.5, -355.6) * mm, "end": v(1130.3, -355.6) * mm, "construction": true});
            skLineSegment(sketch, "E230.1.0.1", {"start": v(2578.1, -355.6) * mm, "end": v(2578.1, -127) * mm});
            skLineSegment(sketch, "E230.1.0.2", {"start": v(2654.3, -355.6) * mm, "end": v(2654.3, -127) * mm});
            skCircle(sketch, "E230.1.0.3", {"center": v(2616.2, -311.15) * mm, "radius": 11.11 * mm});
            skCircle(sketch, "E230.1.0.4", {"center": v(2616.2, -171.45) * mm, "radius": 11.11 * mm});
            skLineSegment(sketch, "E230.1.0.5", {"start": v(2578.1, -355.6) * mm, "end": v(2654.3, -355.6) * mm});
            skLineSegment(sketch, "E230.1.0.6", {"start": v(2578.1, -127) * mm, "end": v(2654.3, -127) * mm});
            skLineSegment(sketch, "E230.direction1", {"start": v(1320.8, -241.3) * mm, "end": v(2768.6, -241.3) * mm, "construction": true});
            skSolve(sketch);
        }
        {
            var Q0;
            Q0=qSketchRegion(id+"F15",true);
            extrude(context, id + "F16", {"entities" : qUnion([Q0]), "operationType" : NewBodyOperationType.ADD, "depth" : 19.05 * mm});
        }
        {
            var Q0;
            Q0=makeQuery(id+"F12.opExtrude","SWEPT_FACE",FACE,{"disambiguationData":[OSD([sQuery(id+"F11.wireOp",EDGE,"E173.MirrorCS")])]});
            var sketch = newSketch(context, id + "F17", { "sketchPlane" : qUnion([Q0])});
            skLineSegment(sketch, "E231", {"start": v(0, -262.73) * mm, "end": v(0, 1224.7) * mm, "construction": true});
            skLineSegment(sketch, "E232.0", {"start": v(-1320.8, 0) * mm, "end": v(1320.8, 0) * mm, "construction": true});
            skLineSegment(sketch, "E233.0", {"start": v(-1320.8, 231.9) * mm, "end": v(1320.8, 231.9) * mm, "construction": true});
            skLineSegment(sketch, "E234.0", {"start": v(-1187.45, -262.73) * mm, "end": v(-1187.45, 1224.7) * mm, "construction": true});
            skLineSegment(sketch, "E235.0", {"start": v(-1320.8, 333.5) * mm, "end": v(1320.8, 333.5) * mm, "construction": true});
            skLineSegment(sketch, "E236.bottom", {"start": v(-1289.05, 435.1) * mm, "end": v(-1085.85, 435.1) * mm});
            skLineSegment(sketch, "E236.top", {"start": v(-1289.05, 231.9) * mm, "end": v(-1085.85, 231.9) * mm});
            skLineSegment(sketch, "E236.left", {"start": v(-1289.05, 435.1) * mm, "end": v(-1289.05, 424.05) * mm});
            skLineSegment(sketch, "E236.right", {"start": v(-1085.85, 435.1) * mm, "end": v(-1085.85, 424.05) * mm});
            skPoint(sketch, "E236.middle", {"position": v(-1187.45, 333.5) * mm});
            skLineSegment(sketch, "E237.0", {"start": v(-1289.05, 424.05) * mm, "end": v(-1197.36, 424.05) * mm});
            skLineSegment(sketch, "E238.MirrorCS", {"start": v(-1289.05, 242.95) * mm, "end": v(-1197.36, 242.95) * mm});
            skLineSegment(sketch, "E239.0", {"start": v(-1183.9, 249.3) * mm, "end": v(-1183.9, 417.7) * mm});
            skLineSegment(sketch, "E240.MirrorCS", {"start": v(-1191, 249.3) * mm, "end": v(-1191, 417.7) * mm});
            skLineSegment(sketch, "E241", {"start": v(-1177.54, 424.05) * mm, "end": v(-1085.85, 424.05) * mm});
            skLineSegment(sketch, "E242", {"start": v(-1177.54, 242.95) * mm, "end": v(-1085.85, 242.95) * mm});
            skPoint(sketch, "E243.newPointB", {"position": v(-1191, 1224.7) * mm});
            skArc(sketch, "E243.filletArc", {"start": v(-1191, 417.7) * mm, "mid": v(-1192.87, 422.2) * mm, "end": v(-1197.36, 424.05) * mm});
            skPoint(sketch, "E244.newPointA", {"position": v(-1191, -262.73) * mm});
            skArc(sketch, "E244.filletArc", {"start": v(-1197.36, 242.95) * mm, "mid": v(-1192.87, 244.81) * mm, "end": v(-1191, 249.3) * mm});
            skPoint(sketch, "E245.newPointA", {"position": v(-1183.9, -262.73) * mm});
            skArc(sketch, "E245.filletArc", {"start": v(-1183.9, 249.3) * mm, "mid": v(-1182.03, 244.81) * mm, "end": v(-1177.54, 242.95) * mm});
            skPoint(sketch, "E246.newPointB", {"position": v(-1183.9, 1224.7) * mm});
            skArc(sketch, "E246.filletArc", {"start": v(-1177.54, 424.05) * mm, "mid": v(-1182.03, 422.2) * mm, "end": v(-1183.9, 417.7) * mm});
            skLineSegment(sketch, "E247.trimOffspring", {"start": v(-1289.05, 242.95) * mm, "end": v(-1289.05, 231.9) * mm});
            skLineSegment(sketch, "E248.trimOffspring", {"start": v(-1085.85, 242.95) * mm, "end": v(-1085.85, 231.9) * mm});
            skArc(sketch, "E249.MirrorCS", {"start": v(1177.54, 424.05) * mm, "mid": v(1182.03, 422.2) * mm, "end": v(1183.9, 417.7) * mm});
            skArc(sketch, "E250.MirrorCS", {"start": v(1183.9, 249.3) * mm, "mid": v(1182.03, 244.81) * mm, "end": v(1177.54, 242.95) * mm});
            skArc(sketch, "E251.MirrorCS", {"start": v(1197.36, 242.95) * mm, "mid": v(1192.87, 244.81) * mm, "end": v(1191, 249.3) * mm});
            skArc(sketch, "E252.MirrorCS", {"start": v(1191, 417.7) * mm, "mid": v(1192.87, 422.2) * mm, "end": v(1197.36, 424.05) * mm});
            skLineSegment(sketch, "E253.MirrorCS", {"start": v(1085.85, 242.95) * mm, "end": v(1085.85, 231.9) * mm});
            skLineSegment(sketch, "E254.MirrorCS", {"start": v(1183.9, 249.3) * mm, "end": v(1183.9, 417.7) * mm});
            skLineSegment(sketch, "E255.MirrorCS", {"start": v(1289.05, 242.95) * mm, "end": v(1289.05, 231.9) * mm});
            skLineSegment(sketch, "E256.MirrorCS", {"start": v(1085.85, 435.1) * mm, "end": v(1085.85, 424.05) * mm});
            skLineSegment(sketch, "E257.MirrorCS", {"start": v(1289.05, 435.1) * mm, "end": v(1289.05, 424.05) * mm});
            skLineSegment(sketch, "E258.MirrorCS", {"start": v(1289.05, 242.95) * mm, "end": v(1197.36, 242.95) * mm});
            skLineSegment(sketch, "E259.MirrorCS", {"start": v(1289.05, 424.05) * mm, "end": v(1197.36, 424.05) * mm});
            skLineSegment(sketch, "E260.MirrorCS", {"start": v(1289.05, 435.1) * mm, "end": v(1085.85, 435.1) * mm});
            skLineSegment(sketch, "E261.MirrorCS", {"start": v(1177.54, 424.05) * mm, "end": v(1085.85, 424.05) * mm});
            skLineSegment(sketch, "E262.MirrorCS", {"start": v(1289.05, 231.9) * mm, "end": v(1085.85, 231.9) * mm});
            skLineSegment(sketch, "E263.MirrorCS", {"start": v(1177.54, 242.95) * mm, "end": v(1085.85, 242.95) * mm});
            skLineSegment(sketch, "E264.MirrorCS", {"start": v(1191, 249.3) * mm, "end": v(1191, 417.7) * mm});
            skPoint(sketch, "E265.MirrorP", {"position": v(1187.45, 333.5) * mm});
            skSolve(sketch);
        }
        {
            var Q0;
            Q0=qSketchRegion(id+"F17",true);
            extrude(context, id + "F18", {"entities" : qUnion([Q0]), "depth" : 401.57 * mm});
        }
        {
            var Q0;
            Q0=makeQuery(id+"F18.opExtrude","SWEPT_FACE",FACE,{"disambiguationData":[OSD([sQuery(id+"F17.wireOp",EDGE,"E236.bottom")])]});
            var sketch = newSketch(context, id + "F19", { "sketchPlane" : qUnion([Q0])});
            skLineSegment(sketch, "E266.bottom", {"start": v(-1289.05, -649.22) * mm, "end": v(-1278, -649.22) * mm});
            skLineSegment(sketch, "E266.top", {"start": v(-1289.05, -446.02) * mm, "end": v(-1278, -446.02) * mm});
            skLineSegment(sketch, "E266.left", {"start": v(-1289.05, -649.22) * mm, "end": v(-1289.05, -446.02) * mm});
            skLineSegment(sketch, "E266.right", {"start": v(-1085.85, -649.22) * mm, "end": v(-1085.85, -446.02) * mm});
            skLineSegment(sketch, "E267", {"start": v(-1187.45, -446.02) * mm, "end": v(-1187.45, -700.9) * mm, "construction": true});
            skLineSegment(sketch, "E268", {"start": v(-1289.05, -547.62) * mm, "end": v(-1023.84, -547.62) * mm, "construction": true});
            skLineSegment(sketch, "E269.0", {"start": v(-1278, -649.22) * mm, "end": v(-1278, -557.53) * mm});
            skLineSegment(sketch, "E270.MirrorCS", {"start": v(-1096.9, -649.22) * mm, "end": v(-1096.9, -557.53) * mm});
            skLineSegment(sketch, "E271.0", {"start": v(-1271.65, -551.18) * mm, "end": v(-1103.25, -551.18) * mm});
            skLineSegment(sketch, "E272.MirrorCS", {"start": v(-1271.65, -544.07) * mm, "end": v(-1103.25, -544.07) * mm});
            skPoint(sketch, "E273.orphan", {"position": v(-1023.84, -551.18) * mm});
            skPoint(sketch, "E274.orphan", {"position": v(-1023.84, -544.07) * mm});
            skLineSegment(sketch, "E275.trimOffspring", {"start": v(-1096.9, -537.72) * mm, "end": v(-1096.9, -446.02) * mm});
            skPoint(sketch, "E276.orphan", {"position": v(-1289.05, -544.07) * mm});
            skLineSegment(sketch, "E277.trimOffspring", {"start": v(-1278, -537.72) * mm, "end": v(-1278, -446.02) * mm});
            skPoint(sketch, "E278.orphan", {"position": v(-1289.05, -551.18) * mm});
            skLineSegment(sketch, "E279.trimOffspring", {"start": v(-1096.9, -446.02) * mm, "end": v(-1085.85, -446.02) * mm});
            skLineSegment(sketch, "E280.trimOffspring", {"start": v(-1096.9, -649.22) * mm, "end": v(-1085.85, -649.22) * mm});
            skPoint(sketch, "E281.visualSharp", {"position": v(-1278, -544.07) * mm});
            skArc(sketch, "E281.filletArc", {"start": v(-1278, -537.72) * mm, "mid": v(-1276.14, -542.2) * mm, "end": v(-1271.65, -544.07) * mm});
            skPoint(sketch, "E282.visualSharp", {"position": v(-1278, -551.18) * mm});
            skArc(sketch, "E282.filletArc", {"start": v(-1271.65, -551.18) * mm, "mid": v(-1276.14, -553.04) * mm, "end": v(-1278, -557.53) * mm});
            skPoint(sketch, "E283.visualSharp", {"position": v(-1096.9, -551.18) * mm});
            skArc(sketch, "E283.filletArc", {"start": v(-1096.9, -557.53) * mm, "mid": v(-1098.76, -553.04) * mm, "end": v(-1103.25, -551.18) * mm});
            skPoint(sketch, "E284.visualSharp", {"position": v(-1096.9, -544.07) * mm});
            skArc(sketch, "E284.filletArc", {"start": v(-1103.25, -544.07) * mm, "mid": v(-1098.76, -542.2) * mm, "end": v(-1096.9, -537.72) * mm});
            skArc(sketch, "E285.MirrorCS", {"start": v(1271.65, -551.18) * mm, "mid": v(1276.14, -553.04) * mm, "end": v(1278, -557.53) * mm});
            skArc(sketch, "E286.MirrorCS", {"start": v(1278, -537.72) * mm, "mid": v(1276.14, -542.2) * mm, "end": v(1271.65, -544.07) * mm});
            skArc(sketch, "E287.MirrorCS", {"start": v(1096.9, -557.53) * mm, "mid": v(1098.76, -553.04) * mm, "end": v(1103.25, -551.18) * mm});
            skArc(sketch, "E288.MirrorCS", {"start": v(1103.25, -544.07) * mm, "mid": v(1098.76, -542.2) * mm, "end": v(1096.9, -537.72) * mm});
            skLineSegment(sketch, "E289.MirrorCS", {"start": v(1289.05, -547.62) * mm, "end": v(1023.84, -547.62) * mm, "construction": true});
            skLineSegment(sketch, "E290.MirrorCS", {"start": v(1096.9, -649.22) * mm, "end": v(1085.85, -649.22) * mm});
            skLineSegment(sketch, "E291.MirrorCS", {"start": v(1289.05, -649.22) * mm, "end": v(1278, -649.22) * mm});
            skLineSegment(sketch, "E292.MirrorCS", {"start": v(1289.05, -446.02) * mm, "end": v(1278, -446.02) * mm});
            skPoint(sketch, "E293.MirrorP", {"position": v(1096.9, -551.18) * mm});
            skLineSegment(sketch, "E294.MirrorCS", {"start": v(1096.9, -446.02) * mm, "end": v(1085.85, -446.02) * mm});
            skPoint(sketch, "E295.MirrorP", {"position": v(1289.05, -544.07) * mm});
            skPoint(sketch, "E296.MirrorP", {"position": v(1278, -551.18) * mm});
            skLineSegment(sketch, "E297.MirrorCS", {"start": v(1271.65, -551.18) * mm, "end": v(1103.25, -551.18) * mm});
            skLineSegment(sketch, "E298.MirrorCS", {"start": v(1289.05, -649.22) * mm, "end": v(1289.05, -446.02) * mm});
            skPoint(sketch, "E299.MirrorP", {"position": v(1289.05, -551.18) * mm});
            skLineSegment(sketch, "E300.MirrorCS", {"start": v(1085.85, -649.22) * mm, "end": v(1085.85, -446.02) * mm});
            skPoint(sketch, "E301.MirrorP", {"position": v(1278, -544.07) * mm});
            skLineSegment(sketch, "E302.MirrorCS", {"start": v(1096.9, -649.22) * mm, "end": v(1096.9, -557.53) * mm});
            skLineSegment(sketch, "E303.MirrorCS", {"start": v(1278, -537.72) * mm, "end": v(1278, -446.02) * mm});
            skLineSegment(sketch, "E304.MirrorCS", {"start": v(1278, -649.22) * mm, "end": v(1278, -557.53) * mm});
            skLineSegment(sketch, "E305.MirrorCS", {"start": v(1271.65, -544.07) * mm, "end": v(1103.25, -544.07) * mm});
            skPoint(sketch, "E306.MirrorP", {"position": v(1096.9, -544.07) * mm});
            skPoint(sketch, "E307.MirrorP", {"position": v(1023.84, -544.07) * mm});
            skLineSegment(sketch, "E308.MirrorCS", {"start": v(1096.9, -537.72) * mm, "end": v(1096.9, -446.02) * mm});
            skLineSegment(sketch, "E309.MirrorCS", {"start": v(1187.45, -446.02) * mm, "end": v(1187.45, -700.9) * mm, "construction": true});
            skPoint(sketch, "E310.MirrorP", {"position": v(1023.84, -551.18) * mm});
            skSolve(sketch);
        }
        {
            var Q0;
            Q0=qSketchRegion(id+"F19",true);
            extrude(context, id + "F20", {"entities" : qUnion([Q0]), "depth" : 292.1 * mm});
        }
        {
            var Q0;
            Q0=makeQuery(id+"F20.opExtrude","CAP_FACE",FACE,{"disambiguationData":[OSD([sQuery(id+"F19.wireOp",EDGE,"E266.bottom"),sQuery(id+"F19.wireOp",EDGE,"E266.top"),sQuery(id+"F19.wireOp",EDGE,"E266.left"),sQuery(id+"F19.wireOp",EDGE,"E266.right"),sQuery(id+"F19.wireOp",EDGE,"E269.0"),sQuery(id+"F19.wireOp",EDGE,"E270.MirrorCS"),sQuery(id+"F19.wireOp",EDGE,"E271.0"),sQuery(id+"F19.wireOp",EDGE,"E272.MirrorCS"),sQuery(id+"F19.wireOp",EDGE,"E275.trimOffspring"),sQuery(id+"F19.wireOp",EDGE,"E277.trimOffspring"),sQuery(id+"F19.wireOp",EDGE,"E279.trimOffspring"),sQuery(id+"F19.wireOp",EDGE,"E280.trimOffspring"),sQuery(id+"F19.wireOp",EDGE,"E281.filletArc"),sQuery(id+"F19.wireOp",EDGE,"E282.filletArc"),sQuery(id+"F19.wireOp",EDGE,"E283.filletArc"),sQuery(id+"F19.wireOp",EDGE,"E284.filletArc")])],"isStart":false});
            var sketch = newSketch(context, id + "F21", { "sketchPlane" : qUnion([Q0])});
            skLineSegment(sketch, "E311.0", {"start": v(-1289.05, -649.22) * mm, "end": v(-1289.05, -446.02) * mm, "construction": true});
            skLineSegment(sketch, "E312.0", {"start": v(-1085.85, -649.22) * mm, "end": v(-1085.85, -446.02) * mm, "construction": true});
            skLineSegment(sketch, "E313", {"start": v(-1289.05, -547.62) * mm, "end": v(-1085.85, -547.62) * mm, "construction": true});
            skLineSegment(sketch, "E314.bottom", {"start": v(-1301.75, -433.32) * mm, "end": v(-1073.15, -433.32) * mm});
            skLineSegment(sketch, "E314.top", {"start": v(-1301.75, -661.92) * mm, "end": v(-1073.15, -661.92) * mm});
            skLineSegment(sketch, "E314.left", {"start": v(-1301.75, -433.32) * mm, "end": v(-1301.75, -661.92) * mm});
            skLineSegment(sketch, "E314.right", {"start": v(-1073.15, -433.32) * mm, "end": v(-1073.15, -661.92) * mm});
            skPoint(sketch, "E314.middle", {"position": v(-1187.45, -547.62) * mm});
            skLineSegment(sketch, "E315", {"start": v(-1187.45, -433.32) * mm, "end": v(-1187.45, -661.92) * mm, "construction": true});
            skLineSegment(sketch, "E316.0", {"start": v(-1289.05, -477.77) * mm, "end": v(-1085.85, -477.77) * mm, "construction": true});
            skCircle(sketch, "E317", {"center": v(-1187.45, -477.77) * mm, "radius": 11.11 * mm});
            skCircle(sketch, "E318.MirrorC", {"center": v(-1187.45, -617.47) * mm, "radius": 11.11 * mm});
            skCircle(sketch, "E319.MirrorC", {"center": v(1187.45, -617.47) * mm, "radius": 11.11 * mm});
            skCircle(sketch, "E320.MirrorC", {"center": v(1187.45, -477.77) * mm, "radius": 11.11 * mm});
            skLineSegment(sketch, "E321.MirrorCS", {"start": v(1289.05, -477.77) * mm, "end": v(1085.85, -477.77) * mm, "construction": true});
            skLineSegment(sketch, "E322.MirrorCS", {"start": v(1289.05, -547.62) * mm, "end": v(1085.85, -547.62) * mm, "construction": true});
            skLineSegment(sketch, "E323.MirrorCS", {"start": v(1289.05, -649.22) * mm, "end": v(1289.05, -446.02) * mm, "construction": true});
            skLineSegment(sketch, "E324.MirrorCS", {"start": v(1187.45, -433.32) * mm, "end": v(1187.45, -661.92) * mm, "construction": true});
            skPoint(sketch, "E325.MirrorP", {"position": v(1187.45, -547.62) * mm});
            skLineSegment(sketch, "E326.MirrorCS", {"start": v(1073.15, -433.32) * mm, "end": v(1073.15, -661.92) * mm});
            skLineSegment(sketch, "E327.MirrorCS", {"start": v(1301.75, -661.92) * mm, "end": v(1073.15, -661.92) * mm});
            skLineSegment(sketch, "E328.MirrorCS", {"start": v(1301.75, -433.32) * mm, "end": v(1073.15, -433.32) * mm});
            skLineSegment(sketch, "E329.MirrorCS", {"start": v(1085.85, -649.22) * mm, "end": v(1085.85, -446.02) * mm, "construction": true});
            skLineSegment(sketch, "E330.MirrorCS", {"start": v(1301.75, -433.32) * mm, "end": v(1301.75, -661.92) * mm});
            skSolve(sketch);
        }
        {
            var Q0;
            Q0=qSketchRegion(id+"F21",true);
            extrude(context, id + "F22", {"entities" : qUnion([Q0]), "depth" : 19.05 * mm});
        }
        {
            var Q0;
            Q0=makeQuery(id+"F20.opExtrude","SWEPT_FACE",FACE,{"disambiguationData":[OSD([sQuery(id+"F19.wireOp",EDGE,"E266.right")])]});
            var sketch = newSketch(context, id + "F23", { "sketchPlane" : qUnion([Q0])});
            skLineSegment(sketch, "E331.0.0", {"start": v(-649.22, 435.1) * mm, "end": v(-446.02, 435.1) * mm, "construction": true});
            skLineSegment(sketch, "E331.0.1", {"start": v(-446.02, 435.1) * mm, "end": v(-446.02, 727.2) * mm, "construction": true});
            skLineSegment(sketch, "E331.0.2", {"start": v(-446.02, 727.2) * mm, "end": v(-649.22, 727.2) * mm, "construction": true});
            skLineSegment(sketch, "E331.0.3", {"start": v(-649.22, 727.2) * mm, "end": v(-649.22, 435.1) * mm, "construction": true});
            skLineSegment(sketch, "E332.0", {"start": v(-446.02, 574.8) * mm, "end": v(-649.22, 574.8) * mm, "construction": true});
            skLineSegment(sketch, "E333", {"start": v(-547.62, 574.8) * mm, "end": v(-547.62, 602) * mm, "construction": true});
            skCircle(sketch, "E334", {"center": v(-547.62, 574.8) * mm, "radius": 44.45 * mm});
            skCircle(sketch, "E335.0", {"center": v(-547.62, 574.8) * mm, "radius": 38.96 * mm});
            skSolve(sketch);
        }
        {
            var Q0;
            Q0=qSketchRegion(id+"F23",true);
            extrude(context, id + "F24", {"entities" : qUnion([Q0]), "depth" : 2171.7 * mm});
        }
        {
            var Q0;
            Q0=makeQuery(id+"F16.opExtrude","CAP_FACE",FACE,{"disambiguationData":[OSD([sQuery(id+"F15.wireOp",EDGE,"E229.1.0.0"),sQuery(id+"F15.wireOp",EDGE,"E229.1.0.1"),sQuery(id+"F15.wireOp",EDGE,"E229.1.0.2"),sQuery(id+"F15.wireOp",EDGE,"E229.1.0.3"),sQuery(id+"F15.wireOp",EDGE,"E229.1.0.4"),sQuery(id+"F15.wireOp",EDGE,"E229.1.0.5")])],"isStart":false});
            var sketch = newSketch(context, id + "F25", { "sketchPlane" : qUnion([Q0])});
            skLineSegment(sketch, "E336.0.0", {"start": v(1130.3, -127) * mm, "end": v(1130.3, -355.6) * mm});
            skLineSegment(sketch, "E336.0.1", {"start": v(1130.3, -355.6) * mm, "end": v(1206.5, -355.6) * mm});
            skLineSegment(sketch, "E336.0.2", {"start": v(1206.5, -355.6) * mm, "end": v(1206.5, -127) * mm});
            skLineSegment(sketch, "E336.0.3", {"start": v(1206.5, -127) * mm, "end": v(1130.3, -127) * mm});
            skCircle(sketch, "E337.0", {"center": v(1168.4, -311.15) * mm, "radius": 11.11 * mm});
            skCircle(sketch, "E338.0", {"center": v(1168.4, -171.45) * mm, "radius": 11.11 * mm});
            skLineSegment(sketch, "E339.0.0", {"start": v(2578.1, -127) * mm, "end": v(2578.1, -355.6) * mm});
            skLineSegment(sketch, "E339.0.1", {"start": v(2578.1, -355.6) * mm, "end": v(2654.3, -355.6) * mm});
            skLineSegment(sketch, "E339.0.2", {"start": v(2654.3, -355.6) * mm, "end": v(2654.3, -127) * mm});
            skLineSegment(sketch, "E339.0.3", {"start": v(2654.3, -127) * mm, "end": v(2578.1, -127) * mm});
            skCircle(sketch, "E340.0", {"center": v(2616.2, -171.45) * mm, "radius": 11.11 * mm});
            skCircle(sketch, "E341.0", {"center": v(2616.2, -311.15) * mm, "radius": 11.11 * mm});
            skSolve(sketch);
        }
        {
            var Q0;
            Q0=qSketchRegion(id+"F25",true);
            extrude(context, id + "F26", {"entities" : qUnion([Q0]), "depth" : 19 * mm});
        }
        {
            var Q0;
            {var subQ7=sQuery(id+"F11.wireOp",EDGE,"E174.trimOffspring");var subQ14=sQuery(id+"F11.wireOp",EDGE,"E169.top");Q0=makeQuery(id+"F16.boolean.opBoolean","SPLIT",FACE,{"disambiguationData":[TD([makeQuery(id+"F12.opExtrude","SWEPT_FACE",FACE,{"disambiguationData":[OSD([subQ7])]})])],"derivedFrom":makeQuery(id+"F12.opExtrude","SWEPT_FACE",FACE,{"disambiguationData":[OSD([subQ14])]})});}
            cPlane(context, id + "F27", {"entities" : qUnion([Q0]), "cplaneType" : CPlaneType.OFFSET, "offset" : 108 * mm, "width" : 150 * mm, "height" : 150 * mm});
        }
        {
            var Q0;
            Q0=qCreatedBy(id+"F27.planeOp",FACE);
            var sketch = newSketch(context, id + "F28", { "sketchPlane" : qUnion([Q0])});
            skLineSegment(sketch, "E342.0", {"start": v(2692.4, -1524.13) * mm, "end": v(2692.4, 788.61) * mm, "construction": true});
            skPoint(sketch, "E343.orphan", {"position": v(2692.4, -114.3) * mm});
            skPoint(sketch, "E344.orphan", {"position": v(2692.4, -368.3) * mm});
            skLineSegment(sketch, "E345.0", {"start": v(948.9, -1524.13) * mm, "end": v(948.9, 788.61) * mm, "construction": true});
            skLineSegment(sketch, "E346.0", {"start": v(1023.9, -1524.13) * mm, "end": v(1023.9, 788.61) * mm, "construction": true});
            skLineSegment(sketch, "E347.0", {"start": v(-1460.5, -368.3) * mm, "end": v(-1460.5, -114.3) * mm, "construction": true});
            skLineSegment(sketch, "E348", {"start": v(-1460.5, -241.3) * mm, "end": v(2900.96, -241.3) * mm, "construction": true});
            skPoint(sketch, "E348.endSnap0", {"position": v(-1460.5, -241.3) * mm});
            skLineSegment(sketch, "E349.bottom", {"start": v(948.9, -51.3) * mm, "end": v(1098.9, -51.3) * mm});
            skLineSegment(sketch, "E349.top", {"start": v(948.9, -431.3) * mm, "end": v(1098.9, -431.3) * mm});
            skLineSegment(sketch, "E349.left", {"start": v(948.9, -51.3) * mm, "end": v(948.9, -431.3) * mm});
            skLineSegment(sketch, "E349.right", {"start": v(1098.9, -51.3) * mm, "end": v(1098.9, -431.3) * mm});
            skPoint(sketch, "E349.middle", {"position": v(1023.9, -241.3) * mm});
            skLineSegment(sketch, "E350.0", {"start": v(-1460.5, -86.3) * mm, "end": v(2900.96, -86.3) * mm, "construction": true});
            skCircle(sketch, "E351", {"center": v(1023.9, -86.3) * mm, "radius": 7.25 * mm});
            skCircle(sketch, "E352.MirrorC", {"center": v(1023.9, -396.3) * mm, "radius": 7.25 * mm});
            skPoint(sketch, "E353.1.0.0", {"position": v(1698.9, -241.3) * mm});
            skLineSegment(sketch, "E353.1.0.1", {"start": v(1773.9, -51.3) * mm, "end": v(1773.9, -431.3) * mm});
            skLineSegment(sketch, "E353.1.0.2", {"start": v(1623.9, -51.3) * mm, "end": v(1773.9, -51.3) * mm});
            skLineSegment(sketch, "E353.1.0.3", {"start": v(1623.9, -431.3) * mm, "end": v(1773.9, -431.3) * mm});
            skLineSegment(sketch, "E353.1.0.4", {"start": v(1623.9, -51.3) * mm, "end": v(1623.9, -431.3) * mm});
            skCircle(sketch, "E353.1.0.5", {"center": v(1698.9, -396.3) * mm, "radius": 7.25 * mm});
            skCircle(sketch, "E353.1.0.6", {"center": v(1698.9, -86.3) * mm, "radius": 7.25 * mm});
            skPoint(sketch, "E353.2.0.0", {"position": v(2373.9, -241.3) * mm});
            skLineSegment(sketch, "E353.2.0.1", {"start": v(2448.9, -51.3) * mm, "end": v(2448.9, -431.3) * mm});
            skLineSegment(sketch, "E353.2.0.2", {"start": v(2298.9, -51.3) * mm, "end": v(2448.9, -51.3) * mm});
            skLineSegment(sketch, "E353.2.0.3", {"start": v(2298.9, -431.3) * mm, "end": v(2448.9, -431.3) * mm});
            skLineSegment(sketch, "E353.2.0.4", {"start": v(2298.9, -51.3) * mm, "end": v(2298.9, -431.3) * mm});
            skCircle(sketch, "E353.2.0.5", {"center": v(2373.9, -396.3) * mm, "radius": 7.25 * mm});
            skCircle(sketch, "E353.2.0.6", {"center": v(2373.9, -86.3) * mm, "radius": 7.25 * mm});
            skLineSegment(sketch, "E353.direction1", {"start": v(1023.9, -241.3) * mm, "end": v(1698.9, -241.3) * mm, "construction": true});
            skPoint(sketch, "E354.0.3.0", {"position": v(3048.9, -241.3) * mm});
            skLineSegment(sketch, "E354.1.3.0", {"start": v(3123.9, -51.3) * mm, "end": v(3123.9, -431.3) * mm});
            skLineSegment(sketch, "E354.4.3.0", {"start": v(2973.9, -51.3) * mm, "end": v(3123.9, -51.3) * mm});
            skLineSegment(sketch, "E354.7.3.0", {"start": v(2973.9, -431.3) * mm, "end": v(3123.9, -431.3) * mm});
            skLineSegment(sketch, "E354.10.3.0", {"start": v(2973.9, -51.3) * mm, "end": v(2973.9, -431.3) * mm});
            skCircle(sketch, "E354.13.3.0", {"center": v(3048.9, -396.3) * mm, "radius": 7.25 * mm});
            skCircle(sketch, "E354.15.3.0", {"center": v(3048.9, -86.3) * mm, "radius": 7.25 * mm});
            skPoint(sketch, "E354.0.4.0", {"position": v(3723.9, -241.3) * mm});
            skLineSegment(sketch, "E354.1.4.0", {"start": v(3798.9, -51.3) * mm, "end": v(3798.9, -431.3) * mm});
            skLineSegment(sketch, "E354.4.4.0", {"start": v(3648.9, -51.3) * mm, "end": v(3798.9, -51.3) * mm});
            skLineSegment(sketch, "E354.7.4.0", {"start": v(3648.9, -431.3) * mm, "end": v(3798.9, -431.3) * mm});
            skLineSegment(sketch, "E354.10.4.0", {"start": v(3648.9, -51.3) * mm, "end": v(3648.9, -431.3) * mm});
            skCircle(sketch, "E354.13.4.0", {"center": v(3723.9, -396.3) * mm, "radius": 7.25 * mm});
            skCircle(sketch, "E354.15.4.0", {"center": v(3723.9, -86.3) * mm, "radius": 7.25 * mm});
            skSolve(sketch);
        }
        {
            var Q0;
            Q0=qSketchRegion(id+"F28",true);
            extrude(context, id + "F29", {"entities" : qUnion([Q0]), "oppositeDirection" : true, "depth" : 19 * mm});
        }
        {
            var Q0;
            Q0=makeQuery(id+"F26.opExtrude","SWEPT_FACE",FACE,{"disambiguationData":[OSD([sQuery(id+"F25.wireOp",EDGE,"E336.0.1")])]});
            var Q1;
            Q1=makeQuery(id+"F26.opExtrude","SWEPT_FACE",FACE,{"disambiguationData":[OSD([sQuery(id+"F25.wireOp",EDGE,"E336.0.3")])]});
            cPlane(context, id + "F30", {"entities" : qUnion([Q0, Q1]), "cplaneType" : CPlaneType.MID_PLANE, "offset" : 150 * mm, "width" : 150 * mm, "height" : 150 * mm});
        }
        {
            var Q0;
            Q0=qCreatedBy(id+"F10.planeOp",FACE);
            var sketch = newSketch(context, id + "F31", { "sketchPlane" : qUnion([Q0])});
            skLineSegment(sketch, "E355.0.0", {"start": v(-368.3, 231.65) * mm, "end": v(-368.3, 217.42) * mm, "construction": true});
            skLineSegment(sketch, "E355.0.1", {"start": v(-368.3, 217.42) * mm, "end": v(-114.3, 217.42) * mm, "construction": true});
            skLineSegment(sketch, "E355.0.2", {"start": v(-114.3, 217.42) * mm, "end": v(-114.3, 231.65) * mm, "construction": true});
            skLineSegment(sketch, "E355.0.3", {"start": v(-114.3, 231.65) * mm, "end": v(-228.6, 231.65) * mm, "construction": true});
            skArc(sketch, "E355.0.4", {"start": v(-228.6, 231.65) * mm, "mid": v(-233.1, 233.5) * mm, "end": v(-234.95, 238) * mm, "construction": true});
            skLineSegment(sketch, "E355.0.5", {"start": v(-234.95, 238) * mm, "end": v(-234.95, 450.85) * mm, "construction": true});
            skArc(sketch, "E355.0.6", {"start": v(-234.95, 450.85) * mm, "mid": v(-233.1, 455.34) * mm, "end": v(-228.6, 457.2) * mm, "construction": true});
            skLineSegment(sketch, "E355.0.7", {"start": v(-228.6, 457.2) * mm, "end": v(-114.3, 457.2) * mm, "construction": true});
            skLineSegment(sketch, "E355.0.8", {"start": v(-114.3, 457.2) * mm, "end": v(-114.3, 471.42) * mm, "construction": true});
            skLineSegment(sketch, "E355.0.9", {"start": v(-114.3, 471.42) * mm, "end": v(-368.3, 471.42) * mm, "construction": true});
            skLineSegment(sketch, "E355.0.10", {"start": v(-368.3, 471.42) * mm, "end": v(-368.3, 457.2) * mm, "construction": true});
            skLineSegment(sketch, "E355.0.11", {"start": v(-368.3, 457.2) * mm, "end": v(-254, 457.2) * mm, "construction": true});
            skArc(sketch, "E355.0.12", {"start": v(-254, 457.2) * mm, "mid": v(-249.5, 455.34) * mm, "end": v(-247.65, 450.85) * mm, "construction": true});
            skLineSegment(sketch, "E355.0.13", {"start": v(-247.65, 450.85) * mm, "end": v(-247.65, 238) * mm, "construction": true});
            skArc(sketch, "E355.0.14", {"start": v(-247.65, 238) * mm, "mid": v(-249.5, 233.5) * mm, "end": v(-254, 231.65) * mm, "construction": true});
            skLineSegment(sketch, "E355.0.15", {"start": v(-254, 231.65) * mm, "end": v(-368.3, 231.65) * mm, "construction": true});
            skLineSegment(sketch, "E356.bottom", {"start": v(-368.3, 464.31) * mm, "end": v(-114.3, 464.31) * mm});
            skLineSegment(sketch, "E356.top", {"start": v(-368.3, 224.54) * mm, "end": v(-114.3, 224.54) * mm});
            skLineSegment(sketch, "E356.left", {"start": v(-368.3, 464.31) * mm, "end": v(-368.3, 224.54) * mm});
            skLineSegment(sketch, "E356.right", {"start": v(-114.3, 464.31) * mm, "end": v(-114.3, 224.54) * mm});
            skLineSegment(sketch, "E357", {"start": v(-368.3, 344.42) * mm, "end": v(-114.3, 344.42) * mm, "construction": true});
            skLineSegment(sketch, "E358.0", {"start": v(-368.3, 424.42) * mm, "end": v(-114.3, 424.42) * mm, "construction": true});
            skLineSegment(sketch, "E359.0", {"start": v(-318.3, 464.31) * mm, "end": v(-318.3, 224.54) * mm, "construction": true});
            skLineSegment(sketch, "E360.MirrorCS", {"start": v(-368.3, 264.42) * mm, "end": v(-114.3, 264.42) * mm, "construction": true});
            skCircle(sketch, "E361", {"center": v(-318.3, 424.42) * mm, "radius": 10 * mm});
            skCircle(sketch, "E362", {"center": v(-318.3, 344.42) * mm, "radius": 10 * mm});
            skCircle(sketch, "E363", {"center": v(-318.3, 264.42) * mm, "radius": 10 * mm});
            skLineSegment(sketch, "E364", {"start": v(-241.3, 471.42) * mm, "end": v(-241.3, 217.42) * mm, "construction": true});
            skCircle(sketch, "E365.MirrorC", {"center": v(-164.3, 264.42) * mm, "radius": 10 * mm});
            skCircle(sketch, "E366.MirrorC", {"center": v(-164.3, 424.42) * mm, "radius": 10 * mm});
            skCircle(sketch, "E367.MirrorC", {"center": v(-164.3, 344.42) * mm, "radius": 10 * mm});
            skSolve(sketch);
        }
        {
            var Q0;
            Q0=qSketchRegion(id+"F31",true);
            extrude(context, id + "F32", {"entities" : qUnion([Q0]), "depth" : 19 * mm});
        }
        {
            var Q0;
            Q0=makeQuery(id+"F32.opExtrude","CAP_FACE",FACE,{"disambiguationData":[OSD([sQuery(id+"F31.wireOp",EDGE,"E356.bottom"),sQuery(id+"F31.wireOp",EDGE,"E356.top"),sQuery(id+"F31.wireOp",EDGE,"E356.left"),sQuery(id+"F31.wireOp",EDGE,"E356.right"),sQuery(id+"F31.wireOp",EDGE,"E361"),sQuery(id+"F31.wireOp",EDGE,"E362"),sQuery(id+"F31.wireOp",EDGE,"E363"),sQuery(id+"F31.wireOp",EDGE,"E365.MirrorC"),sQuery(id+"F31.wireOp",EDGE,"E366.MirrorC"),sQuery(id+"F31.wireOp",EDGE,"E367.MirrorC")])],"isStart":false});
            var sketch = newSketch(context, id + "F33", { "sketchPlane" : qUnion([Q0])});
            skLineSegment(sketch, "E368.0.0", {"start": v(-114.3, 464.31) * mm, "end": v(-368.3, 464.31) * mm});
            skLineSegment(sketch, "E368.0.1", {"start": v(-368.3, 464.31) * mm, "end": v(-368.3, 224.54) * mm});
            skLineSegment(sketch, "E368.0.2", {"start": v(-368.3, 224.54) * mm, "end": v(-114.3, 224.54) * mm});
            skLineSegment(sketch, "E368.0.3", {"start": v(-114.3, 224.54) * mm, "end": v(-114.3, 464.31) * mm});
            skCircle(sketch, "E369.0", {"center": v(-318.3, 424.42) * mm, "radius": 10 * mm});
            skCircle(sketch, "E370.0", {"center": v(-318.3, 344.42) * mm, "radius": 10 * mm});
            skCircle(sketch, "E371.0", {"center": v(-318.3, 264.42) * mm, "radius": 10 * mm});
            skCircle(sketch, "E372.0", {"center": v(-164.3, 264.42) * mm, "radius": 10 * mm});
            skCircle(sketch, "E373.0", {"center": v(-164.3, 344.42) * mm, "radius": 10 * mm});
            skCircle(sketch, "E374.0", {"center": v(-164.3, 424.42) * mm, "radius": 10 * mm});
            skSolve(sketch);
        }
        {
            var Q0;
            Q0=qSketchRegion(id+"F33",true);
            extrude(context, id + "F34", {"entities" : qUnion([Q0]), "depth" : 19 * mm});
        }
        {
            var Q0;
            Q0=qCreatedBy(id+"F30.planeOp",FACE);
            var sketch = newSketch(context, id + "F35", { "sketchPlane" : qUnion([Q0])});
            skLineSegment(sketch, "E375.0", {"start": v(948.9, 560.42) * mm, "end": v(1098.9, 560.42) * mm, "construction": true});
            skLineSegment(sketch, "E376.0", {"start": v(2973.9, 560.42) * mm, "end": v(3123.9, 560.42) * mm, "construction": true});
            skLineSegment(sketch, "E377.0", {"start": v(3648.9, 560.42) * mm, "end": v(3798.9, 560.42) * mm, "construction": true});
            skLineSegment(sketch, "E378.0", {"start": v(2730.4, 464.31) * mm, "end": v(2730.4, 224.54) * mm, "construction": true});
            skLineSegment(sketch, "E379", {"start": v(948.9, 560.42) * mm, "end": v(3798.9, 560.42) * mm});
            skLineSegment(sketch, "E380.0", {"start": v(1130.3, 509.47) * mm, "end": v(1206.5, 509.47) * mm, "construction": true});
            skLineSegment(sketch, "E381", {"start": v(3798.9, 560.42) * mm, "end": v(3798.9, 224.54) * mm});
            skLineSegment(sketch, "E382", {"start": v(3798.9, 224.54) * mm, "end": v(2730.4, 224.54) * mm});
            skLineSegment(sketch, "E383", {"start": v(948.9, 560.42) * mm, "end": v(948.9, 509.47) * mm});
            skLineSegment(sketch, "E384", {"start": v(948.9, 509.47) * mm, "end": v(2720.4, 509.47) * mm});
            skLineSegment(sketch, "E385", {"start": v(2730.4, 499.47) * mm, "end": v(2730.4, 464.31) * mm});
            skLineSegment(sketch, "E386", {"start": v(2730.4, 464.31) * mm, "end": v(2730.4, 224.54) * mm});
            skPoint(sketch, "E387.visualSharp", {"position": v(2730.4, 509.47) * mm});
            skArc(sketch, "E387.filletArc", {"start": v(2730.4, 499.47) * mm, "mid": v(2727.47, 506.55) * mm, "end": v(2720.4, 509.47) * mm});
            skSolve(sketch);
        }
        {
            var Q0;
            Q0=qSketchRegion(id+"F35",true);
            extrude(context, id + "F36", {"entities" : qUnion([Q0]), "endBound" : BoundingType.SYMMETRIC, "depth" : 12.5 * mm});
        }
        {
            var Q0;
            Q0=makeQuery(id+"F26.opExtrude","SWEPT_FACE",FACE,{"disambiguationData":[OSD([sQuery(id+"F25.wireOp",EDGE,"E336.0.1")])]});
            var sketch = newSketch(context, id + "F37", { "sketchPlane" : qUnion([Q0])});
            skLineSegment(sketch, "E388.0.0", {"start": v(3798.9, 560.42) * mm, "end": v(948.9, 560.42) * mm});
            skLineSegment(sketch, "E388.0.1", {"start": v(948.9, 560.42) * mm, "end": v(948.9, 509.47) * mm});
            skLineSegment(sketch, "E388.0.2", {"start": v(948.9, 509.47) * mm, "end": v(2720.4, 509.47) * mm});
            skArc(sketch, "E388.0.3", {"start": v(2720.4, 509.47) * mm, "mid": v(2727.47, 506.55) * mm, "end": v(2730.4, 499.47) * mm});
            skLineSegment(sketch, "E388.0.4", {"start": v(2730.4, 499.47) * mm, "end": v(2730.4, 224.54) * mm});
            skLineSegment(sketch, "E388.0.5", {"start": v(2730.4, 224.54) * mm, "end": v(3798.9, 224.54) * mm});
            skLineSegment(sketch, "E388.0.6", {"start": v(3798.9, 224.54) * mm, "end": v(3798.9, 560.42) * mm});
            skSolve(sketch);
        }
        {
            var Q0;
            Q0=qSketchRegion(id+"F37",true);
            extrude(context, id + "F38", {"entities" : qUnion([Q0]), "endBound" : BoundingType.SYMMETRIC, "depth" : 12.5 * mm});
        }
        {
            var Q0;
            Q0=makeQuery(id+"F36.opExtrude","SWEPT_EDGE",EDGE,{"disambiguationData":[OSD([sQuery(id+"F35.wireOp",EDGE,"E381"),sQuery(id+"F35.wireOp",EDGE,"E382")])]});
            var Q1;
            Q1=makeQuery(id+"F38.opExtrude","SWEPT_EDGE",EDGE,{"disambiguationData":[OSD([sQuery(id+"F37.wireOp",EDGE,"E388.0.5"),sQuery(id+"F37.wireOp",EDGE,"E388.0.6")])]});
            chamfer(context, id + "F39", {"entities" : qUnion([Q0, Q1]), "chamferType" : ChamferType.TWO_OFFSETS, "width1" : 300 * mm, "oppositeDirection" : false, "width2" : 600 * mm, "tangentPropagation" : true});
        }
        {
            var Q0;
            Q0=makeQuery(id+"F38.opExtrude","SWEPT_BODY",BODY,{"disambiguationData":[OSD([sQuery(id+"F37.wireOp",EDGE,"E388.0.0"),sQuery(id+"F37.wireOp",EDGE,"E388.0.1"),sQuery(id+"F37.wireOp",EDGE,"E388.0.2"),sQuery(id+"F37.wireOp",EDGE,"E388.0.3"),sQuery(id+"F37.wireOp",EDGE,"E388.0.4"),sQuery(id+"F37.wireOp",EDGE,"E388.0.5"),sQuery(id+"F37.wireOp",EDGE,"E388.0.6")])]});
            var Q1;
            Q1=qCreatedBy(id+"F30.planeOp",FACE);
            mirror(context, id + "F40", {"entities" : qUnion([Q0]), "mirrorPlane" : qUnion([Q1])});
        }
        {
            var Q0;
            Q0=makeQuery(id+"F36.opExtrude","SWEPT_EDGE",EDGE,{"disambiguationData":[OSD([sQuery(id+"F35.wireOp",EDGE,"E383"),sQuery(id+"F35.wireOp",EDGE,"E384")])]});
            var Q1;
            Q1=makeQuery(id+"F40.opPattern","COPY",EDGE,{"derivedFrom":makeQuery(id+"F38.opExtrude","SWEPT_EDGE",EDGE,{"disambiguationData":[OSD([sQuery(id+"F37.wireOp",EDGE,"E388.0.1"),sQuery(id+"F37.wireOp",EDGE,"E388.0.2")])]}),"instanceName":"1"});
            var Q2;
            Q2=makeQuery(id+"F38.opExtrude","SWEPT_EDGE",EDGE,{"disambiguationData":[OSD([sQuery(id+"F37.wireOp",EDGE,"E388.0.1"),sQuery(id+"F37.wireOp",EDGE,"E388.0.2")])]});
            chamfer(context, id + "F41", {"entities" : qUnion([Q0, Q1, Q2]), "width" : 40 * mm, "tangentPropagation" : true});
        }
        {
            var Q0;
            Q0=makeQuery(id+"F38.opExtrude","SWEPT_BODY",BODY,{"disambiguationData":[OSD([sQuery(id+"F37.wireOp",EDGE,"E388.0.0"),sQuery(id+"F37.wireOp",EDGE,"E388.0.1"),sQuery(id+"F37.wireOp",EDGE,"E388.0.2"),sQuery(id+"F37.wireOp",EDGE,"E388.0.3"),sQuery(id+"F37.wireOp",EDGE,"E388.0.4"),sQuery(id+"F37.wireOp",EDGE,"E388.0.5"),sQuery(id+"F37.wireOp",EDGE,"E388.0.6")])]});
            var Q1;
            Q1=makeQuery(id+"F34.opExtrude","SWEPT_BODY",BODY,{"disambiguationData":[OSD([sQuery(id+"F33.wireOp",EDGE,"E368.0.0"),sQuery(id+"F33.wireOp",EDGE,"E368.0.1"),sQuery(id+"F33.wireOp",EDGE,"E368.0.2"),sQuery(id+"F33.wireOp",EDGE,"E368.0.3"),sQuery(id+"F33.wireOp",EDGE,"E369.0"),sQuery(id+"F33.wireOp",EDGE,"E370.0"),sQuery(id+"F33.wireOp",EDGE,"E371.0"),sQuery(id+"F33.wireOp",EDGE,"E372.0"),sQuery(id+"F33.wireOp",EDGE,"E373.0"),sQuery(id+"F33.wireOp",EDGE,"E374.0")])]});
            var Q2;
            Q2=makeQuery(id+"F29.opExtrude","SWEPT_BODY",BODY,{"disambiguationData":[OSD([sQuery(id+"F28.wireOp",EDGE,"E354.1.4.0"),sQuery(id+"F28.wireOp",EDGE,"E354.4.4.0"),sQuery(id+"F28.wireOp",EDGE,"E354.7.4.0"),sQuery(id+"F28.wireOp",EDGE,"E354.10.4.0"),sQuery(id+"F28.wireOp",EDGE,"E354.13.4.0"),sQuery(id+"F28.wireOp",EDGE,"E354.15.4.0")])]});
            var Q3;
            Q3=makeQuery(id+"F29.opExtrude","SWEPT_BODY",BODY,{"disambiguationData":[OSD([sQuery(id+"F28.wireOp",EDGE,"E354.1.3.0"),sQuery(id+"F28.wireOp",EDGE,"E354.4.3.0"),sQuery(id+"F28.wireOp",EDGE,"E354.7.3.0"),sQuery(id+"F28.wireOp",EDGE,"E354.10.3.0"),sQuery(id+"F28.wireOp",EDGE,"E354.13.3.0"),sQuery(id+"F28.wireOp",EDGE,"E354.15.3.0")])]});
            var Q4;
            Q4=makeQuery(id+"F29.opExtrude","SWEPT_BODY",BODY,{"disambiguationData":[OSD([sQuery(id+"F28.wireOp",EDGE,"E353.2.0.1"),sQuery(id+"F28.wireOp",EDGE,"E353.2.0.2"),sQuery(id+"F28.wireOp",EDGE,"E353.2.0.3"),sQuery(id+"F28.wireOp",EDGE,"E353.2.0.4"),sQuery(id+"F28.wireOp",EDGE,"E353.2.0.5"),sQuery(id+"F28.wireOp",EDGE,"E353.2.0.6")])]});
            var Q5;
            Q5=makeQuery(id+"F29.opExtrude","SWEPT_BODY",BODY,{"disambiguationData":[OSD([sQuery(id+"F28.wireOp",EDGE,"E353.1.0.1"),sQuery(id+"F28.wireOp",EDGE,"E353.1.0.2"),sQuery(id+"F28.wireOp",EDGE,"E353.1.0.3"),sQuery(id+"F28.wireOp",EDGE,"E353.1.0.4"),sQuery(id+"F28.wireOp",EDGE,"E353.1.0.5"),sQuery(id+"F28.wireOp",EDGE,"E353.1.0.6")])]});
            var Q6;
            Q6=makeQuery(id+"F29.opExtrude","SWEPT_BODY",BODY,{"disambiguationData":[OSD([sQuery(id+"F28.wireOp",EDGE,"E349.bottom"),sQuery(id+"F28.wireOp",EDGE,"E349.top"),sQuery(id+"F28.wireOp",EDGE,"E349.left"),sQuery(id+"F28.wireOp",EDGE,"E349.right"),sQuery(id+"F28.wireOp",EDGE,"E351"),sQuery(id+"F28.wireOp",EDGE,"E352.MirrorC")])]});
            var Q7;
            Q7=makeQuery(id+"F36.opExtrude","SWEPT_BODY",BODY,{"disambiguationData":[OSD([sQuery(id+"F35.wireOp",EDGE,"E379"),sQuery(id+"F35.wireOp",EDGE,"E381"),sQuery(id+"F35.wireOp",EDGE,"E382"),sQuery(id+"F35.wireOp",EDGE,"E383"),sQuery(id+"F35.wireOp",EDGE,"E384"),sQuery(id+"F35.wireOp",EDGE,"E385"),sQuery(id+"F35.wireOp",EDGE,"E386"),sQuery(id+"F35.wireOp",EDGE,"E387.filletArc")])]});
            var Q8;
            Q8=makeQuery(id+"F40.opPattern","COPY",BODY,{"derivedFrom":makeQuery(id+"F38.opExtrude","SWEPT_BODY",BODY,{"disambiguationData":[OSD([sQuery(id+"F37.wireOp",EDGE,"E388.0.0"),sQuery(id+"F37.wireOp",EDGE,"E388.0.1"),sQuery(id+"F37.wireOp",EDGE,"E388.0.2"),sQuery(id+"F37.wireOp",EDGE,"E388.0.3"),sQuery(id+"F37.wireOp",EDGE,"E388.0.4"),sQuery(id+"F37.wireOp",EDGE,"E388.0.5"),sQuery(id+"F37.wireOp",EDGE,"E388.0.6")])]}),"instanceName":"1"});
            var Q9;
            Q9=makeQuery(id+"F26.opExtrude","SWEPT_BODY",BODY,{"disambiguationData":[OSD([sQuery(id+"F25.wireOp",EDGE,"E336.0.0"),sQuery(id+"F25.wireOp",EDGE,"E336.0.1"),sQuery(id+"F25.wireOp",EDGE,"E336.0.2"),sQuery(id+"F25.wireOp",EDGE,"E336.0.3"),sQuery(id+"F25.wireOp",EDGE,"E337.0"),sQuery(id+"F25.wireOp",EDGE,"E338.0")])]});
            var Q10;
            Q10=makeQuery(id+"F26.opExtrude","SWEPT_BODY",BODY,{"disambiguationData":[OSD([sQuery(id+"F25.wireOp",EDGE,"E339.0.0"),sQuery(id+"F25.wireOp",EDGE,"E339.0.1"),sQuery(id+"F25.wireOp",EDGE,"E339.0.2"),sQuery(id+"F25.wireOp",EDGE,"E339.0.3"),sQuery(id+"F25.wireOp",EDGE,"E340.0"),sQuery(id+"F25.wireOp",EDGE,"E341.0")])]});
            booleanBodies(context, id + "F42", {"operationType" : BooleanOperationType.UNION, "tools" : qUnion([Q0, Q1, Q2, Q3, Q4, Q5, Q6, Q7, Q8, Q9, Q10])});
        }
        {
            var Q0;
            {var subQ0=makeQuery(id+"F38.opExtrude","SWEPT_FACE",FACE,{"disambiguationData":[OSD([sQuery(id+"F37.wireOp",EDGE,"E388.0.5")])]});Q0=makeQuery(id+"F42.opBoolean","MERGE",FACE,{"derivedFrom":[makeQuery(id+"F34.opExtrude","SWEPT_FACE",FACE,{"disambiguationData":[OSD([sQuery(id+"F33.wireOp",EDGE,"E368.0.2")])]}),makeQuery(id+"F36.opExtrude","SWEPT_FACE",FACE,{"disambiguationData":[OSD([sQuery(id+"F35.wireOp",EDGE,"E382")])]}),subQ0,makeQuery(id+"F40.opPattern","COPY",FACE,{"derivedFrom":subQ0,"instanceName":"1"})]});}
            var sketch = newSketch(context, id + "F43", { "sketchPlane" : qUnion([Q0])});
            skLineSegment(sketch, "E389.0.0", {"start": v(2730.4, 349.35) * mm, "end": v(3198.9, 349.35) * mm, "construction": true});
            skLineSegment(sketch, "E389.0.1", {"start": v(3198.9, 349.35) * mm, "end": v(3198.9, 361.85) * mm, "construction": true});
            skLineSegment(sketch, "E389.0.2", {"start": v(3198.9, 361.85) * mm, "end": v(2730.4, 361.85) * mm, "construction": true});
            skLineSegment(sketch, "E389.0.3", {"start": v(2730.4, 361.85) * mm, "end": v(2730.4, 368.3) * mm, "construction": true});
            skLineSegment(sketch, "E389.0.4", {"start": v(2730.4, 368.3) * mm, "end": v(2711.4, 368.3) * mm, "construction": true});
            skLineSegment(sketch, "E389.0.5", {"start": v(2711.4, 368.3) * mm, "end": v(2711.4, 114.3) * mm, "construction": true});
            skLineSegment(sketch, "E389.0.6", {"start": v(2711.4, 114.3) * mm, "end": v(2730.4, 114.3) * mm, "construction": true});
            skLineSegment(sketch, "E389.0.7", {"start": v(2730.4, 114.3) * mm, "end": v(2730.4, 120.75) * mm, "construction": true});
            skLineSegment(sketch, "E389.0.8", {"start": v(2730.4, 120.75) * mm, "end": v(3198.9, 120.75) * mm, "construction": true});
            skLineSegment(sketch, "E389.0.9", {"start": v(3198.9, 120.75) * mm, "end": v(3198.9, 133.25) * mm, "construction": true});
            skLineSegment(sketch, "E389.0.10", {"start": v(3198.9, 133.25) * mm, "end": v(2730.4, 133.25) * mm, "construction": true});
            skLineSegment(sketch, "E389.0.11", {"start": v(2730.4, 133.25) * mm, "end": v(2730.4, 235.05) * mm, "construction": true});
            skLineSegment(sketch, "E389.0.12", {"start": v(2730.4, 235.05) * mm, "end": v(3198.9, 235.05) * mm, "construction": true});
            skLineSegment(sketch, "E389.0.13", {"start": v(3198.9, 235.05) * mm, "end": v(3198.9, 247.55) * mm, "construction": true});
            skLineSegment(sketch, "E389.0.14", {"start": v(3198.9, 247.55) * mm, "end": v(2730.4, 247.55) * mm, "construction": true});
            skLineSegment(sketch, "E389.0.15", {"start": v(2730.4, 247.55) * mm, "end": v(2730.4, 349.35) * mm, "construction": true});
            skPoint(sketch, "E390.oppositeSnap0", {"position": v(3198.9, 127) * mm});
            skLineSegment(sketch, "E390.bottom", {"start": v(3198.9, 355.6) * mm, "end": v(3048.9, 355.6) * mm});
            skLineSegment(sketch, "E390.top", {"start": v(3198.9, 127) * mm, "end": v(3048.9, 127) * mm});
            skLineSegment(sketch, "E390.left", {"start": v(3198.9, 355.6) * mm, "end": v(3198.9, 127) * mm});
            skLineSegment(sketch, "E390.right", {"start": v(3048.9, 355.6) * mm, "end": v(3048.9, 127) * mm});
            skSolve(sketch);
        }
        {
            var Q0;
            Q0=qSketchRegion(id+"F43",true);
            extrude(context, id + "F44", {"entities" : qUnion([Q0]), "operationType" : NewBodyOperationType.ADD, "depth" : 12.5 * mm});
        }
        {
            var Q0;
            Q0=makeQuery(id+"F32.opExtrude","SWEPT_BODY",BODY,{"disambiguationData":[OSD([sQuery(id+"F31.wireOp",EDGE,"E356.bottom"),sQuery(id+"F31.wireOp",EDGE,"E356.top"),sQuery(id+"F31.wireOp",EDGE,"E356.left"),sQuery(id+"F31.wireOp",EDGE,"E356.right"),sQuery(id+"F31.wireOp",EDGE,"E361"),sQuery(id+"F31.wireOp",EDGE,"E362"),sQuery(id+"F31.wireOp",EDGE,"E363"),sQuery(id+"F31.wireOp",EDGE,"E365.MirrorC"),sQuery(id+"F31.wireOp",EDGE,"E366.MirrorC"),sQuery(id+"F31.wireOp",EDGE,"E367.MirrorC")])]});
            deleteBodies(context, id + "F45", {"entities" : qUnion([Q0])});
        }
        {
            var Q0;
            Q0=makeQuery(id+"F5.opExtrude","SWEPT_BODY",BODY,{"disambiguationData":[OSD([sQuery(id+"F4.wireOp",EDGE,"E87.bottom"),sQuery(id+"F4.wireOp",EDGE,"E87.top"),sQuery(id+"F4.wireOp",EDGE,"E87.left"),sQuery(id+"F4.wireOp",EDGE,"E87.right"),sQuery(id+"F4.wireOp",EDGE,"E89.0"),sQuery(id+"F4.wireOp",EDGE,"E90.MirrorCS"),sQuery(id+"F4.wireOp",EDGE,"E91.0"),sQuery(id+"F4.wireOp",EDGE,"E92.0"),sQuery(id+"F4.wireOp",EDGE,"E93.trimOffspring"),sQuery(id+"F4.wireOp",EDGE,"E94.trimOffspring"),sQuery(id+"F4.wireOp",EDGE,"E95.trimOffspring"),sQuery(id+"F4.wireOp",EDGE,"E96.trimOffspring"),sQuery(id+"F4.wireOp",EDGE,"E97.filletArc"),sQuery(id+"F4.wireOp",EDGE,"E98.filletArc"),sQuery(id+"F4.wireOp",EDGE,"E99.filletArc"),sQuery(id+"F4.wireOp",EDGE,"E100.filletArc")])]});
            deleteBodies(context, id + "F46", {"entities" : qUnion([Q0])});
        }
    });
